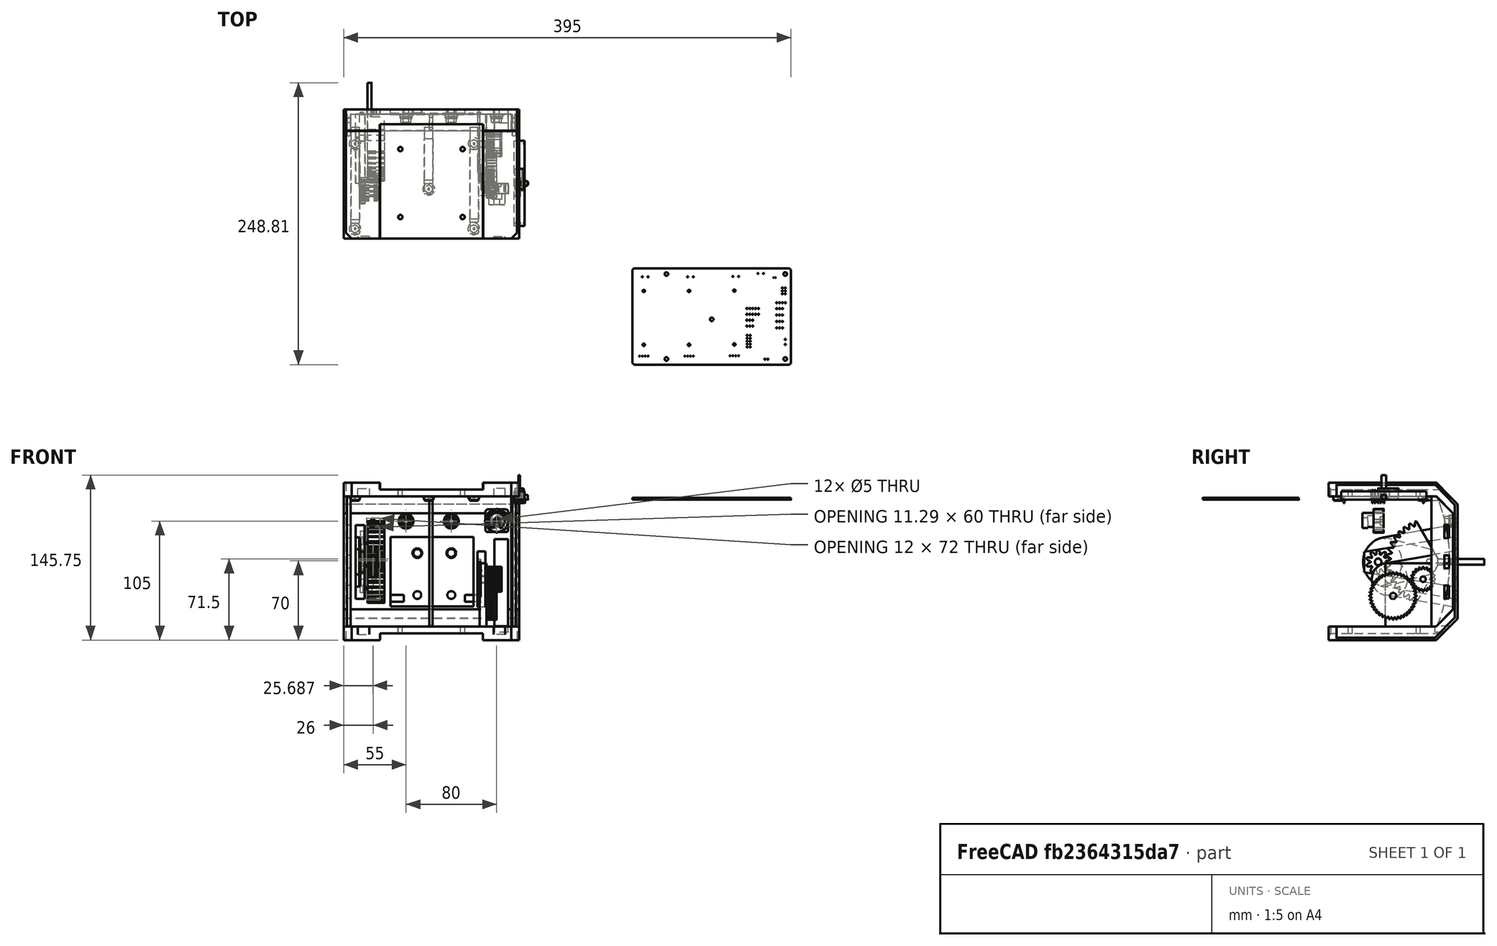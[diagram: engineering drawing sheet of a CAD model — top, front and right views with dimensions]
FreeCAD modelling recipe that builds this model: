
FCSTD DOCUMENT  (FreeCAD 0.19R24276 (Git))
Label: C152QuadrantCase
License: All rights reserved
LicenseURL: http://en.wikipedia.org/wiki/All_rights_reserved
objects: Sketcher::SketchObject×71, Part::Feature×60, App::Part×60, PartDesign::Pocket×42, PartDesign::Pad×29, PartDesign::Plane×15, PartDesign::Body×12, PartDesign::Fillet×10, PartDesign::Chamfer×8, Part::Part2DObjectPython×4, Mesh::Feature×3, PartDesign::ShapeBinder×2, PartDesign::LinearPattern×1, PartDesign::Line×1, PartDesign::PolarPattern×1
note: 345 computed .brp shape members not serialized (recipe doc carries the construction recipe); baked Part::Feature solids carry a one-line shape summary decoded from their .brp

FEATURE [Sketcher::SketchObject] Sketch
  FullyConstrained = false
  MapMode = 5
  Placement = pos=(0,0,0) rot=(0.57735,0.57735,0.57735;2.0944rad)
  Support = -> [YZ_Plane050]
  sketch-geometry (12):
    g0: LineSegment StartX=-48.736 StartY=3 StartZ=0 EndX=46.264 EndY=3 EndZ=0
    g1: LineSegment StartX=46.264 StartY=3 StartZ=0 EndX=61.264 EndY=-12 EndZ=0
    g2: LineSegment StartX=61.264 StartY=-12 StartZ=0 EndX=61.264 EndY=-97 EndZ=0
    g3: LineSegment StartX=61.264 StartY=-97 StartZ=0 EndX=46.264 EndY=-112 EndZ=0
    g4: LineSegment StartX=46.264 StartY=-112 StartZ=0 EndX=-48.736 EndY=-112 EndZ=0
    g5: LineSegment StartX=-48.736 StartY=3 StartZ=0 EndX=-48.736 EndY=15 EndZ=0
    g6: LineSegment StartX=-48.736 StartY=15 StartZ=0 EndX=46.264 EndY=15 EndZ=0
    g7: LineSegment StartX=46.264 StartY=15 StartZ=0 EndX=65.264 EndY=-4 EndZ=0
    g8: LineSegment StartX=65.264 StartY=-4 StartZ=0 EndX=65.264 EndY=-105 EndZ=0
    g9: LineSegment StartX=65.264 StartY=-105 StartZ=0 EndX=46.264 EndY=-124 EndZ=0
    g10: LineSegment StartX=46.264 StartY=-124 StartZ=0 EndX=-48.736 EndY=-124 EndZ=0
    g11: LineSegment StartX=-48.736 StartY=-124 StartZ=0 EndX=-48.736 EndY=-112 EndZ=0
  constraints (35):
    c: Horizontal(g0)
    c: Coincident(g1,g0)
    c: Coincident(g2,g1)
    c: Vertical(g2)
    c: Coincident(g3,g2)
    c: Coincident(g4,g3)
    c: Horizontal(g4)
    c: DistanceY(g2,g2) = 85
    c: DistanceY(g1,g0) = 15
    c: DistanceX(g0,g1) = 15
    c: DistanceY(g3,g2) = 15
    c: DistanceX(g3,g2) = 15
    c: DistanceX(g0,g0) = 95
    c: Equal(g0,g4)
    c: Coincident(g5,g0)
    c: Vertical(g5)
    c: Coincident(g6,g5)
    c: Horizontal(g6)
    c: Coincident(g7,g6)
    c: Coincident(g8,g7)
    c: Vertical(g8)
    c: Coincident(g9,g8)
    c: Coincident(g10,g9)
    c: Horizontal(g10)
    c: Coincident(g11,g4)
    c: Vertical(g11)
    c: Coincident(g11,g10)
    c: DistanceY(g11,g11) = 12
    c: Equal(g5,g11)
    c: Equal(g10,g4)
    c: Equal(g0,g6)
    c: DistanceX(g1,g7) = 4
    c: DistanceY(g-1,g0) = 3
    c: Parallel(g3,g9)
    c: Parallel(g1,g7)
FEATURE [PartDesign::Pad] Pad
  Direction = (1,1,1)
  Length = 155
  Length2 = 100
  Placement = pos=(0,0,0) rot=(0.57735,0.57735,0.57735;2.0944rad)
  Profile = -> Sketch
  Reversed = true
  Type = 0
FEATURE [Sketcher::SketchObject] Sketch001
  ExternalGeometry = -> [Pad]
  FullyConstrained = false
  MapMode = 5
  Placement = pos=(2.87e-14,65.264,-1.44e-14) rot=(0.57735,0.57735,0.57735;4.18879rad)
  Support = -> [Pad]
  sketch-geometry (39):
    g0: Circle CenterX=-19 CenterY=-20 CenterZ=0 NormalX=0 NormalY=0 NormalZ=1 AngleXU=0 Radius=2.5
    g1: LineSegment StartX=-9 StartY=-30 StartZ=0 EndX=-9 EndY=-10 EndZ=0
    g2: LineSegment StartX=-9 StartY=-10 StartZ=0 EndX=-29 EndY=-10 EndZ=0
    g3: LineSegment StartX=-29 StartY=-10 StartZ=0 EndX=-29 EndY=-30 EndZ=0
    g4: LineSegment StartX=-29 StartY=-30 StartZ=0 EndX=-9 EndY=-30 EndZ=0
    g5: Circle CenterX=-19 CenterY=-20 CenterZ=0 NormalX=0 NormalY=0 NormalZ=1 AngleXU=0 Radius=14.1421
    g6: Circle CenterX=-19 CenterY=-60 CenterZ=0 NormalX=0 NormalY=0 NormalZ=1 AngleXU=0 Radius=2.5
    g7: Circle CenterX=-19 CenterY=-100 CenterZ=0 NormalX=0 NormalY=0 NormalZ=1 AngleXU=0 Radius=2.5
    g8: LineSegment StartX=-117 StartY=-10 StartZ=0 EndX=-35.015 EndY=-10 EndZ=0
    g9: LineSegment StartX=-35.015 StartY=-10 StartZ=0 EndX=-35.015 EndY=-22 EndZ=0
    g10: LineSegment StartX=-35.015 StartY=-22 StartZ=0 EndX=-117 EndY=-22 EndZ=0
    g11: LineSegment StartX=-117 StartY=-22 StartZ=0 EndX=-117 EndY=-10 EndZ=0
    g12: Circle CenterX=-47.2303 CenterY=-60 CenterZ=0 NormalX=0 NormalY=0 NormalZ=1 AngleXU=0 Radius=4.25
    g13: Circle CenterX=-47.2303 CenterY=-90 CenterZ=0 NormalX=0 NormalY=0 NormalZ=1 AngleXU=0 Radius=4.25
    g14: LineSegment StartX=-16.5 StartY=-123 StartZ=0 EndX=-16.5 EndY=-135 EndZ=0
    g15: LineSegment StartX=-16.5 StartY=-135 StartZ=0 EndX=-88.5 EndY=-135 EndZ=0
    g16: LineSegment StartX=-88.5 StartY=-135 StartZ=0 EndX=-88.5 EndY=-129 EndZ=0
    g17: LineSegment StartX=-88.5 StartY=-129 StartZ=0 EndX=-70.5 EndY=-129 EndZ=0
    g18: LineSegment StartX=-70.5 StartY=-129 StartZ=0 EndX=-70.5 EndY=-126 EndZ=0
    g19: LineSegment StartX=-70.5 StartY=-126 StartZ=0 EndX=-52.5 EndY=-126 EndZ=0
    g20: LineSegment StartX=-52.5 StartY=-126 StartZ=0 EndX=-52.5 EndY=-123 EndZ=0
    g21: LineSegment StartX=-52.5 StartY=-123 StartZ=0 EndX=-34.5 EndY=-123 EndZ=0
    g22: LineSegment StartX=-34.5 StartY=-123 StartZ=0 EndX=-16.5 EndY=-123 EndZ=0
    g23: LineSegment StartX=-47.2303 StartY=-60 StartZ=0 EndX=-84.2303 EndY=-60 EndZ=0
    g24: LineSegment StartX=-84.2303 StartY=-60 StartZ=0 EndX=-84.2303 EndY=-90 EndZ=0
    g25: LineSegment StartX=-84.2303 StartY=-90 StartZ=0 EndX=-47.2303 EndY=-90 EndZ=0
    g26: LineSegment StartX=-47.2303 StartY=-90 StartZ=0 EndX=-47.2303 EndY=-60 EndZ=0
    g27: Circle CenterX=-84.2303 CenterY=-60 CenterZ=0 NormalX=0 NormalY=0 NormalZ=1 AngleXU=0 Radius=3.45
    g28: Circle CenterX=-84.2303 CenterY=-90 CenterZ=0 NormalX=0 NormalY=0 NormalZ=1 AngleXU=0 Radius=3.45
    g29: LineSegment StartX=-84.2303 StartY=-47.9735 StartZ=0 EndX=-90.2303 EndY=-47.9735 EndZ=0
    g30: LineSegment StartX=-90.2303 StartY=-47.9735 StartZ=0 EndX=-90.2303 EndY=-35.9735 EndZ=0
    g31: LineSegment StartX=-90.2303 StartY=-35.9735 StartZ=0 EndX=-84.2303 EndY=-35.9735 EndZ=0
    g32: LineSegment StartX=-84.2303 StartY=-35.9735 StartZ=0 EndX=-84.2303 EndY=-47.9735 EndZ=0
    g33: LineSegment StartX=-84.2303 StartY=-102.026 StartZ=0 EndX=-90.2303 EndY=-102.026 EndZ=0
    g34: LineSegment StartX=-90.2303 StartY=-102.026 StartZ=0 EndX=-90.2303 EndY=-114.026 EndZ=0
    g35: LineSegment StartX=-90.2303 StartY=-114.026 StartZ=0 EndX=-84.2303 EndY=-114.026 EndZ=0
    g36: LineSegment StartX=-84.2303 StartY=-114.026 StartZ=0 EndX=-84.2303 EndY=-102.026 EndZ=0
    g37: LineSegment StartX=-84.2303 StartY=-60 StartZ=0 EndX=-84.2303 EndY=-47.9735 EndZ=0
    g38: LineSegment StartX=-84.2303 StartY=-90 StartZ=0 EndX=-84.2303 EndY=-102.026 EndZ=0
  constraints (107):
    c: DistanceY(g0,g-4) = 20
    c: Coincident(g1,g2)
    c: Coincident(g2,g3)
    c: Coincident(g3,g4)
    c: Coincident(g4,g1)
    c: Equal(g1,g2)
    c: Equal(g1,g3)
    c: Equal(g1,g4)
    c: PointOnObject(g1,g5)
    c: PointOnObject(g2,g5)
    c: PointOnObject(g3,g5)
    c: PointOnObject(g4,g5)
    c: Coincident(g5,g0)
    c: Horizontal(g2)
    c: DistanceX(g0,g-4) = 15
    c: DistanceX(g4,g4) = 20
    c: Radius(g0) = 2.5
    c: Equal(g0,g6)
    c: Equal(g6,g7)
    c: DistanceX(g0,g6) = 0
    c: DistanceX(g6,g7) = 0
    c: DistanceY(g6,g0) = 40
    c: DistanceY(g7,g6) = 40
    c: Coincident(g8,g9)
    c: Coincident(g9,g10)
    c: Coincident(g10,g11)
    c: Coincident(g11,g8)
    c: Horizontal(g8)
    c: Horizontal(g10)
    c: Vertical(g9)
    c: Vertical(g11)
    c: DistanceX(g8,g-4) = 12
    c: DistanceY(g11,g11) = 12
    c: DistanceY(g8,g-4) = 10
    c: DistanceY(g12,g6) = 0
    c: DistanceX(g12,g13) = 0
    c: DistanceY(g13,g12) = 30
    c: Equal(g12,g13)
    c: Radius(g13) = 4.25
    c: Vertical(g14)
    c: Coincident(g15,g14)
    c: Horizontal(g15)
    c: Coincident(g16,g15)
    c: Vertical(g16)
    c: Coincident(g17,g16)
    c: Horizontal(g17)
    c: Vertical(g18)
    c: Coincident(g19,g18)
    c: Horizontal(g19)
    c: Coincident(g20,g19)
    c: Coincident(g21,g20)
    c: Horizontal(g21)
    c: Coincident(g22,g14)
    c: Horizontal(g22)
    c: Vertical(g20)
    c: Equal(g19,g21)
    c: Equal(g21,g22)
    c: Equal(g22,g17)
    c: Coincident(g17,g18)
    c: DistanceX(g15,g15) = 72
    c: DistanceY(g-3,g14) = 20
    c: DistanceX(g14,g-3) = 12.5
    c: Coincident(g21,g22)
    c: Equal(g18,g20)
    c: DistanceY(g18,g18) = 3
    c: DistanceY(g16,g16) = 6
    c: Coincident(g23,g24)
    c: Coincident(g24,g25)
    c: Coincident(g25,g26)
    c: Coincident(g26,g23)
    c: Horizontal(g23)
    c: Horizontal(g25)
    c: Vertical(g24)
    c: Coincident(g23,g12)
    c: Coincident(g25,g13)
    c: DistanceX(g23,g23) = 37
    c: Coincident(g27,g23)
    c: Coincident(g28,g24)
    c: Radius(g28) = 3.45
    c: Equal(g28,g27)
    c: Coincident(g29,g30)
    c: Coincident(g30,g31)
    c: Coincident(g31,g32)
    c: Coincident(g32,g29)
    c: Horizontal(g29)
    c: Horizontal(g31)
    c: Vertical(g30)
    c: Vertical(g32)
    c: Coincident(g33,g34)
    c: Coincident(g34,g35)
    c: Coincident(g35,g36)
    c: Coincident(g36,g33)
    c: Horizontal(g33)
    c: Horizontal(g35)
    c: Vertical(g34)
    c: Vertical(g36)
    c: Equal(g36,g32)
    c: Equal(g31,g33)
    c: Coincident(g37,g27)
    c: Coincident(g37,g29)
    c: Coincident(g38,g28)
    c: Coincident(g38,g33)
    c: Vertical(g38)
    c: Vertical(g37)
    c: Equal(g37,g38)
    c: DistanceY(g32,g32) = 12
    c: DistanceX(g31,g31) = 6
FEATURE [Mesh::Feature] Cessna_trim_wheel
  Placement = pos=(-19,36,-70) rot=(0,1,0;1.5708rad)
FEATURE [PartDesign::Pocket] Pocket
  BaseFeature = -> Pad
  Length = 20
  Length2 = 100
  Placement = pos=(0,0,0) rot=(0.57735,0.57735,0.57735;2.0944rad)
  Profile = -> Sketch001
  Type = 0
FEATURE [Sketcher::SketchObject] Sketch002
  AttachmentOffset = pos=(0,0,-120) rot=(0,0,1;0rad)
  ExternalGeometry = -> [Pocket]
  FullyConstrained = false
  MapMode = 5
  Placement = pos=(-35,7.5e-15,-7.5e-15) rot=(0.57735,0.57735,-0.57735;4.18879rad)
  Support = -> [Pocket]
  sketch-geometry (5):
    g0: LineSegment StartX=61.264 StartY=56.1492 StartZ=0 EndX=61.264 EndY=97 EndZ=0
    g1: LineSegment StartX=46.264 StartY=112 StartZ=0 EndX=1.26399 EndY=112 EndZ=0
    g2: LineSegment StartX=1.26399 StartY=112 StartZ=0 EndX=1.26399 EndY=56.1492 EndZ=0
    g3: LineSegment StartX=61.264 StartY=56.1492 StartZ=0 EndX=1.26399 EndY=56.1492 EndZ=0
    g4: LineSegment StartX=46.264 StartY=112 StartZ=0 EndX=61.264 EndY=97 EndZ=0
  constraints (12):
    c: PointOnObject(g0,g-3)
    c: Coincident(g0,g-4)
    c: Coincident(g1,g-5)
    c: Coincident(g2,g1)
    c: Vertical(g2)
    c: Coincident(g3,g0)
    c: Coincident(g3,g2)
    c: Horizontal(g3)
    c: DistanceX(g3,g3) = 60
    c: PointOnObject(g1,g-5)
    c: Coincident(g4,g1)
    c: Coincident(g4,g0)
FEATURE [PartDesign::Pad] Pad001
  BaseFeature = -> Pocket
  Direction = (1,1,1)
  Length = 6
  Length2 = 100
  Placement = pos=(0,0,0) rot=(0.57735,0.57735,0.57735;2.0944rad)
  Profile = -> Sketch002
  Reversed = true
  Type = 0
FEATURE [Part::Part2DObjectPython] InvoluteGear  label="TrimSmallGear"  # Draft 2D object (typed FeaturePython)
  ExternalGear = true
  HighPrecision = true
  Modules = 1
  NumberOfTeeth = 20
  Placement = pos=(-29,34.7,-70.25) rot=(0,1,0;1.5708rad)
  PressureAngle = 27
FEATURE [PartDesign::Pad] Pad002
  Direction = (1,1,1)
  Length = 13.5
  Length2 = 100
  Placement = pos=(-29,34.7,-70.25) rot=(0,1,0;1.5708rad)
  Profile = -> InvoluteGear
  Type = 0
FEATURE [Part::Part2DObjectPython] InvoluteGear001  # Draft 2D object (typed FeaturePython)
  ExternalGear = true
  HighPrecision = true
  Modules = 1
  NumberOfTeeth = 40
  Placement = pos=(-29,8.2,-85) rot=(0,1,0;1.5708rad)
  PressureAngle = 27
FEATURE [PartDesign::Pad] Pad003
  Direction = (1,1,1)
  Length = 9
  Length2 = 100
  Placement = pos=(-29,8.2,-85) rot=(0,1,0;1.5708rad)
  Profile = -> InvoluteGear001
  Type = 0
FEATURE [Sketcher::SketchObject] Sketch003
  FullyConstrained = true
  MapMode = 5
  Placement = pos=(-29,8.2,-85) rot=(0.707107,0,-0.707107;3.14159rad)
  Support = -> [Pad003]
  sketch-geometry (1):
    g0: Circle CenterX=0 CenterY=0 CenterZ=0 NormalX=0 NormalY=0 NormalZ=1 AngleXU=0 Radius=2.75
  constraints (2):
    c: Coincident(g0,g-1)
    c: Radius(g0) = 2.75
FEATURE [PartDesign::Pocket] Pocket001
  BaseFeature = -> Pad003
  Length = 10
  Length2 = 100
  Placement = pos=(-29,8.2,-85) rot=(0,1,0;1.5708rad)
  Profile = -> Sketch003
  Type = 0
FEATURE [PartDesign::Body] Body002  label="TrimLargeGearBody"
  Group = -> [InvoluteGear001,Pad003,Sketch003,Pocket001]
  Origin = -> Origin052
  Tip = -> Pocket001
FEATURE [Sketcher::SketchObject] Sketch004
  FullyConstrained = true
  MapMode = 5
  Placement = pos=(-15.5,34.7,-70.25) rot=(0,1,0;1.5708rad)
  Support = -> [Pad002]
  sketch-geometry (1):
    g0: Circle CenterX=0 CenterY=0 CenterZ=0 NormalX=0 NormalY=0 NormalZ=1 AngleXU=0 Radius=2.425
  constraints (2):
    c: Coincident(g0,g-1)
    c: Radius(g0) = 2.425
FEATURE [PartDesign::Pocket] Pocket002
  BaseFeature = -> Pad002
  Length = 15
  Length2 = 100
  Placement = pos=(-29,34.7,-70.25) rot=(0,1,0;1.5708rad)
  Profile = -> Sketch004
  Type = 0
FEATURE [PartDesign::Plane] DatumPlane
  AttachmentOffset = pos=(0,0,-13) rot=(0,0,1;0rad)
  Length = 88.036
  MapMode = 7
  Placement = pos=(-16,42.9375,-65.4383) rot=(0.57735,-0.57735,-0.57735;2.0944rad)
  ResizeMode = 0
  Support = -> [Pocket002]
  Width = 123.586
FEATURE [PartDesign::Body] Body  label="TrimSmallGearBody"
  Group = -> [InvoluteGear,Pad002,Sketch004,Pocket002,DatumPlane]
  Origin = -> Origin051
  Tip = -> Pocket002
FEATURE [Mesh::Feature] Mesh  label="TrimSmallGearBody (Meshed)"
FEATURE [Mesh::Feature] Union
FEATURE [Part::Part2DObjectPython] InvoluteGear002  # Draft 2D object (typed FeaturePython)
  ExternalGear = true
  HighPrecision = true
  Modules = 1.8
  NumberOfTeeth = 40
  Placement = pos=(-134,40,-55) rot=(0,1,0;1.5708rad)
  PressureAngle = 27
FEATURE [PartDesign::Pad] Pad004
  Direction = (1,1,1)
  Length = 15
  Length2 = 100
  Placement = pos=(-134,40,-55) rot=(0,1,0;1.5708rad)
  Profile = -> InvoluteGear002
  Type = 0
FEATURE [Sketcher::SketchObject] Sketch005
  ExternalGeometry = -> [Pad004]
  FullyConstrained = false
  MapMode = 5
  Placement = pos=(-134,40,-55) rot=(0.707107,0,-0.707107;3.14159rad)
  Support = -> [Pad004]
  sketch-geometry (9):
    g0: Circle CenterX=0 CenterY=0 CenterZ=0 NormalX=0 NormalY=0 NormalZ=1 AngleXU=0 Radius=2.5
    g1: LineSegment StartX=-36.0831 StartY=11.2641 StartZ=0 EndX=-2.5 EndY=-7.97211 EndZ=0
    g2: LineSegment StartX=36.0831 StartY=11.2641 StartZ=0 EndX=2.5 EndY=-7.97211 EndZ=0
    g3: LineSegment StartX=-36.0831 StartY=11.2641 StartZ=0 EndX=-54.9276 EndY=-6.77916 EndZ=0
    g4: LineSegment StartX=-54.9276 StartY=-6.77916 StartZ=0 EndX=-2.5 EndY=-49.2175 EndZ=0
    g5: LineSegment StartX=-2.5 StartY=-49.2175 StartZ=0 EndX=-2.5 EndY=-7.97211 EndZ=0
    g6: LineSegment StartX=2.5 StartY=-7.97211 StartZ=0 EndX=2.5 EndY=-49.2175 EndZ=0
    g7: LineSegment StartX=2.5 StartY=-49.2175 StartZ=0 EndX=46.3022 EndY=-15.9819 EndZ=0
    g8: LineSegment StartX=46.3022 StartY=-15.9819 StartZ=0 EndX=36.0831 EndY=11.2641 EndZ=0
  constraints (16):
    c: Coincident(g0,g-1)
    c: Radius(g0) = 2.5
    c: Coincident(g1,g-3)
    c: Coincident(g2,g-4)
    c: Symmetric(g1,g2,g-2)
    c: Coincident(g3,g1)
    c: Coincident(g4,g3)
    c: Coincident(g5,g4)
    c: Coincident(g5,g1)
    c: Vertical(g5)
    c: Coincident(g6,g2)
    c: Coincident(g7,g6)
    c: Coincident(g8,g7)
    c: Coincident(g8,g2)
    c: Symmetric(g4,g6,g-2)
    c: DistanceX(g1,g2) = 5
FEATURE [PartDesign::Pocket] Pocket003
  BaseFeature = -> Pad004
  Length = 20
  Length2 = 100
  Placement = pos=(-134,40,-55) rot=(0,1,0;1.5708rad)
  Profile = -> Sketch005
  Type = 0
FEATURE [Sketcher::SketchObject] Sketch006
  ExternalGeometry = -> [Pocket003]
  FullyConstrained = true
  MapMode = 5
  Placement = pos=(-134,40,-55) rot=(0.707107,0,-0.707107;3.14159rad)
  Support = -> [Pocket003]
  sketch-geometry (4):
    g0: LineSegment StartX=-2.5 StartY=-33.8136 StartZ=0 EndX=2.5 EndY=-33.8136 EndZ=0
    g1: LineSegment StartX=2.5 StartY=-33.8136 StartZ=0 EndX=2.5 EndY=-48.8136 EndZ=0
    g2: LineSegment StartX=2.5 StartY=-48.8136 StartZ=0 EndX=-2.5 EndY=-48.8136 EndZ=0
    g3: LineSegment StartX=-2.5 StartY=-48.8136 StartZ=0 EndX=-2.5 EndY=-33.8136 EndZ=0
  constraints (10):
    c: Coincident(g0,g1)
    c: Coincident(g1,g2)
    c: Coincident(g2,g3)
    c: Coincident(g3,g0)
    c: Horizontal(g2)
    c: Vertical(g1)
    c: Vertical(g3)
    c: Coincident(g0,g-3)
    c: Coincident(g0,g-4)
    c: DistanceY(g1,g1) = 15
FEATURE [PartDesign::Pad] Pad005
  BaseFeature = -> Pocket003
  Direction = (1,1,1)
  Length = 15
  Length2 = 100
  Placement = pos=(-134,40,-55) rot=(0,1,0;1.5708rad)
  Profile = -> Sketch006
  Reversed = true
  Type = 0
FEATURE [Part::Part2DObjectPython] InvoluteGear003  # Draft 2D object (typed FeaturePython)
  ExternalGear = true
  HighPrecision = true
  Modules = 1.8
  NumberOfTeeth = 10
  Placement = pos=(-140,-5,-55) rot=(0,1,0;1.5708rad)
  PressureAngle = 27
FEATURE [PartDesign::Pad] Pad006
  Direction = (1,1,1)
  Length = 15
  Length2 = 100
  Placement = pos=(-140,-5,-55) rot=(0,1,0;1.5708rad)
  Profile = -> InvoluteGear003
  Type = 0
FEATURE [Sketcher::SketchObject] Sketch008
  ExternalGeometry = -> [Pad005]
  FullyConstrained = false
  MapMode = 5
  Placement = pos=(-134,88.8136,-55) rot=(0.57735,0.57735,0.57735;4.18879rad)
  Support = -> [Pad005]
  sketch-geometry (4):
    g0: LineSegment StartX=2.5 StartY=15 StartZ=0 EndX=-2.5 EndY=15 EndZ=0
    g1: LineSegment StartX=-2.5 StartY=15 StartZ=0 EndX=-2.5 EndY=3.5 EndZ=0
    g2: LineSegment StartX=-2.5 StartY=3.5 StartZ=0 EndX=2.5 EndY=3.5 EndZ=0
    g3: LineSegment StartX=2.5 StartY=3.5 StartZ=0 EndX=2.5 EndY=15 EndZ=0
  constraints (10):
    c: Coincident(g0,g1)
    c: Coincident(g1,g2)
    c: Coincident(g2,g3)
    c: Coincident(g3,g0)
    c: Horizontal(g2)
    c: Vertical(g1)
    c: Vertical(g3)
    c: Coincident(g0,g-4)
    c: Coincident(g0,g-3)
    c: DistanceY(g-5,g1) = 3.5
FEATURE [PartDesign::Pocket] Pocket005
  BaseFeature = -> Pad005
  Length = 30
  Length2 = 100
  Placement = pos=(-134,40,-55) rot=(0,1,0;1.5708rad)
  Profile = -> Sketch008
  Type = 0
FEATURE [PartDesign::Fillet] Fillet
  Base = -> Pocket005 [Edge322,Edge311,Edge323,Edge301]
  BaseFeature = -> Pocket005
  Placement = pos=(-134,40,-55) rot=(0,1,0;1.5708rad)
  Radius = 1.5
  SupportTransform = false
FEATURE [PartDesign::Body] Body003  label="FlapsLeverWheel"
  Group = -> [InvoluteGear002,Pad004,Sketch005,Pocket003,Sketch006,Pad005,Sketch008,Pocket005,Fillet]
  Origin = -> Origin053
  Tip = -> Fillet
FEATURE [Sketcher::SketchObject] Sketch009
  FullyConstrained = true
  MapMode = 5
  Placement = pos=(-140,-5,-55) rot=(0.707107,0,-0.707107;3.14159rad)
  Support = -> [Pad006]
  sketch-geometry (1):
    g0: Circle CenterX=0 CenterY=0 CenterZ=0 NormalX=0 NormalY=0 NormalZ=1 AngleXU=0 Radius=2.875
  constraints (2):
    c: Coincident(g0,g-1)
    c: Radius(g0) = 2.875
FEATURE [PartDesign::Pocket] Pocket006
  BaseFeature = -> Pad006
  Length = 20
  Length2 = 100
  Placement = pos=(-140,-5,-55) rot=(0,1,0;1.5708rad)
  Profile = -> Sketch009
  Type = 0
FEATURE [PartDesign::Body] Body004  label="FlapsPotWheel"
  Group = -> [InvoluteGear003,Pad006,Sketch009,Pocket006]
  Origin = -> Origin054
  Tip = -> Pocket006
FEATURE [Sketcher::SketchObject] Sketch010
  AttachmentOffset = pos=(0,0,-19) rot=(0,0,1;0rad)
  ExternalGeometry = -> [Pad001]
  FullyConstrained = false
  MapMode = 5
  Placement = pos=(-136,2.99e-14,-2.99e-14) rot=(0.57735,0.57735,-0.57735;4.18879rad)
  Support = -> [Pad001]
  sketch-geometry (7):
    g0: LineSegment StartX=-17.4237 StartY=64.0314 StartZ=0 EndX=61.264 EndY=76.6336 EndZ=0
    g1: LineSegment StartX=61.264 StartY=33.3706 StartZ=0 EndX=61.264 EndY=76.6336 EndZ=0
    g2: LineSegment StartX=61.264 StartY=33.3706 StartZ=0 EndX=-17.4237 EndY=45.9729 EndZ=0
    g3: LineSegment StartX=-17.4237 StartY=45.9729 StartZ=0 EndX=-17.4237 EndY=64.0314 EndZ=0
    g4: LineSegment StartX=94.0604 StartY=55.0021 StartZ=0 EndX=-36.649 EndY=55.0021 EndZ=0
    g5: Circle CenterX=-5.01144 CenterY=55.0021 CenterZ=0 NormalX=0 NormalY=0 NormalZ=1 AngleXU=0 Radius=3.00681
    g6: Circle CenterX=39.9756 CenterY=55.0021 CenterZ=0 NormalX=0 NormalY=0 NormalZ=1 AngleXU=0 Radius=2.57688
  constraints (17):
    c: PointOnObject(g0,g-3)
    c: PointOnObject(g1,g-3)
    c: Coincident(g1,g0)
    c: Vertical(g1)
    c: Coincident(g2,g1)
    c: Coincident(g3,g2)
    c: Coincident(g3,g0)
    c: Vertical(g3)
    c: Horizontal(g4)
    c: Symmetric(g2,g0,g4)
    c: Symmetric(g1,g0,g4)
    c: PointOnObject(g5,g4)
    c: PointOnObject(g6,g4)
    c: Symmetric(g0,g2,g4)
    c: PointOnObject(g0,g-4)
    c: PointOnObject(g1,g-4)
    c: Symmetric(g0,g1,g4)
FEATURE [PartDesign::Pad] Pad007
  BaseFeature = -> Pad001
  Direction = (1,1,1)
  Length = 5.5
  Length2 = 100
  Placement = pos=(0,0,0) rot=(0.57735,0.57735,0.57735;2.0944rad)
  Profile = -> Sketch010
  Type = 0
FEATURE [Part::Feature] Part__Feature  label="SOLID"
  shape: bbox 9.2 x 75 x 24.75 mm, 23 faces (baked)
FEATURE [App::Part] ALPS_RS6011SY_Body  label="ALPS-RS6011SY-Body"
  Group = -> [Part__Feature]
  Origin = -> Origin055
  Placement = pos=(190,-117.2,1.65) rot=(0,0,1;0rad)
FEATURE [Part::Feature] Part__Feature001  label="SOLID001"
  shape: bbox 9.2 x 75 x 24.75 mm, 23 faces (baked)
FEATURE [App::Part] ALPS_RS6011SY_Body001  label="ALPS-RS6011SY-Body001"
  Group = -> [Part__Feature001]
  Origin = -> Origin056
  Placement = pos=(110,-117.5,1.65) rot=(0,0,1;0rad)
FEATURE [Part::Feature] Part__Feature002  label="SOLID002"
  shape: bbox 9.2 x 75 x 24.75 mm, 23 faces (baked)
FEATURE [App::Part] ALPS_RS6011SY_Body002  label="ALPS-RS6011SY-Body002"
  Group = -> [Part__Feature002]
  Origin = -> Origin057
  Placement = pos=(150,-117.5,1.65) rot=(0,0,1;0rad)
FEATURE [Part::Feature] Part__Feature003  label="SOLID003"
  shape: bbox 1.6 x 0.8 x 0.8 mm, 28 faces (baked)
FEATURE [App::Part] C_0603_1608Metric
  Group = -> [Part__Feature003]
  Origin = -> Origin058
  Placement = pos=(119.5,-86,1.65) rot=(0,0,1;0rad)
FEATURE [Part::Feature] Part__Feature004  label="SOLID004"
  shape: bbox 1.6 x 0.8 x 0.8 mm, 28 faces (baked)
FEATURE [App::Part] C_0603_1608Metric001
  Group = -> [Part__Feature004]
  Origin = -> Origin059
  Placement = pos=(213,-120.6,1.65) rot=(0,0,-1;1.5708rad)
FEATURE [Part::Feature] Part__Feature005  label="SOLID005"
  shape: bbox 1.6 x 0.8 x 0.8 mm, 28 faces (baked)
FEATURE [App::Part] C_0603_1608Metric002
  Group = -> [Part__Feature005]
  Origin = -> Origin060
  Placement = pos=(119.5,-90.75,1.65) rot=(0,0,1;0rad)
FEATURE [Part::Feature] Part__Feature006  label="SOLID006"
  shape: bbox 1.6 x 0.8 x 0.8 mm, 28 faces (baked)
FEATURE [App::Part] C_0603_1608Metric003
  Group = -> [Part__Feature006]
  Origin = -> Origin061
  Placement = pos=(210.4,-120.6,1.65) rot=(0,0,-1;1.5708rad)
FEATURE [Part::Feature] Part__Feature007  label="SOLID007"
  shape: bbox 1.6 x 0.8 x 0.8 mm, 28 faces (baked)
FEATURE [App::Part] C_0603_1608Metric004
  Group = -> [Part__Feature007]
  Origin = -> Origin062
  Placement = pos=(161.2,-83.2,1.65) rot=(0,0,1;0rad)
FEATURE [Part::Feature] Part__Feature008  label="SOLID008"
  shape: bbox 1.6 x 0.8 x 0.8 mm, 28 faces (baked)
FEATURE [App::Part] C_0603_1608Metric005
  Group = -> [Part__Feature008]
  Origin = -> Origin063
  Placement = pos=(161.2,-87.4,1.65) rot=(0,0,1;0rad)
FEATURE [Part::Feature] Part__Feature009  label="SOLID009"
  shape: bbox 1.6 x 0.8 x 0.8 mm, 28 faces (baked)
FEATURE [App::Part] C_0603_1608Metric006
  Group = -> [Part__Feature009]
  Origin = -> Origin064
  Placement = pos=(210.4,-125.6,1.65) rot=(0,0,-1;1.5708rad)
FEATURE [Part::Feature] Part__Feature010  label="SOLID010"
  shape: bbox 1.6 x 0.8 x 0.8 mm, 28 faces (baked)
FEATURE [App::Part] C_0603_1608Metric007
  Group = -> [Part__Feature010]
  Origin = -> Origin065
  Placement = pos=(213.2,-125.6,1.65) rot=(0,0,-1;1.5708rad)
FEATURE [Part::Feature] Part__Feature011  label="SOLID011"
  shape: bbox 1.6 x 0.8 x 0.8 mm, 28 faces (baked)
FEATURE [App::Part] C_0603_1608Metric008
  Group = -> [Part__Feature011]
  Origin = -> Origin066
  Placement = pos=(182,-143,1.65) rot=(0,0,1;3.14159rad)
FEATURE [Part::Feature] Part__Feature012  label="SOLID012"
  shape: bbox 1.6 x 0.8 x 0.8 mm, 28 faces (baked)
FEATURE [App::Part] C_0603_1608Metric009
  Group = -> [Part__Feature012]
  Origin = -> Origin067
  Placement = pos=(182,-146.6,1.65) rot=(0,0,1;3.14159rad)
FEATURE [Part::Feature] Part__Feature013  label="SOLID013"
  shape: bbox 1.6 x 0.8 x 0.8 mm, 28 faces (baked)
FEATURE [App::Part] C_0603_1608Metric010
  Group = -> [Part__Feature013]
  Origin = -> Origin068
  Placement = pos=(218.4,-84.4,1.65) rot=(0,0,1;0rad)
FEATURE [Part::Feature] Part__Feature014  label="SOLID014"
  shape: bbox 1.6 x 0.8 x 0.8 mm, 28 faces (baked)
FEATURE [App::Part] C_0603_1608Metric011
  Group = -> [Part__Feature014]
  Origin = -> Origin069
  Placement = pos=(208.6,-84.4,1.65) rot=(0,0,1;0rad)
FEATURE [Part::Feature] Part__Feature015  label="SOLID015"
  shape: bbox 1.6 x 0.8 x 0.8 mm, 28 faces (baked)
FEATURE [App::Part] C_0603_1608Metric012
  Group = -> [Part__Feature015]
  Origin = -> Origin070
  Placement = pos=(227.35,-85.9,1.65) rot=(0,0,1;0rad)
FEATURE [Part::Feature] Part__Feature016  label="SOLID016"
  shape: bbox 1.6 x 0.8 x 0.8 mm, 28 faces (baked)
FEATURE [App::Part] C_0603_1608Metric013
  Group = -> [Part__Feature016]
  Origin = -> Origin071
  Placement = pos=(223.85,-85.9,1.65) rot=(0,0,1;3.14159rad)
FEATURE [Part::Feature] Part__Feature017  label="SOLID017"
  shape: bbox 1.6 x 0.8 x 0.8 mm, 28 faces (baked)
FEATURE [App::Part] C_0603_1608Metric014
  Group = -> [Part__Feature017]
  Origin = -> Origin072
  Placement = pos=(177.5,-83.25,1.65) rot=(0,0,1;0rad)
FEATURE [Part::Feature] Part__Feature018  label="SOLID018"
  shape: bbox 1.6 x 0.8 x 0.8 mm, 28 faces (baked)
FEATURE [App::Part] C_0603_1608Metric015
  Group = -> [Part__Feature018]
  Origin = -> Origin073
  Placement = pos=(220.938,-105,1.65) rot=(0,0,1;0rad)
FEATURE [Part::Feature] Part__Feature019  label="SOLID019"
  shape: bbox 1.6 x 0.8 x 0.8 mm, 28 faces (baked)
FEATURE [App::Part] C_0603_1608Metric016
  Group = -> [Part__Feature019]
  Origin = -> Origin074
  Placement = pos=(211.2,-98.2,1.65) rot=(0,0,-1;1.5708rad)
FEATURE [Part::Feature] Part__Feature020  label="SOLID020"
  shape: bbox 1.6 x 0.8 x 0.8 mm, 28 faces (baked)
FEATURE [App::Part] C_0603_1608Metric017
  Group = -> [Part__Feature020]
  Origin = -> Origin075
  Placement = pos=(212.2,-88.6,1.65) rot=(0,0,1;3.14159rad)
FEATURE [Part::Feature] Part__Feature021  label="SOLID021"
  shape: bbox 1.6 x 0.8 x 0.8 mm, 28 faces (baked)
FEATURE [App::Part] C_0603_1608Metric018
  Group = -> [Part__Feature021]
  Origin = -> Origin076
  Placement = pos=(228.6,-93.8,1.65) rot=(0,0,1;1.5708rad)
FEATURE [Part::Feature] Part__Feature022  label="SOLID022"
  shape: bbox 2.54 x 7.62 x 11.54 mm, 76 faces (baked)
FEATURE [App::Part] PinHeader_1x03_P2_54mm_Vertical  label="PinHeader_1x03_P2.54mm_Vertical"
  Group = -> [Part__Feature022]
  Origin = -> Origin077
  Placement = pos=(232.5,-110.6,1.65) rot=(0,0,-1;1.5708rad)
FEATURE [Part::Feature] Part__Feature023  label="SOLID023"
  shape: bbox 2.54 x 7.62 x 11.54 mm, 76 faces (baked)
FEATURE [App::Part] PinHeader_1x03_P2_54mm_Vertical001  label="PinHeader_1x03_P2.54mm_Vertical001"
  Group = -> [Part__Feature023]
  Origin = -> Origin078
  Placement = pos=(232.5,-116.267,1.65) rot=(0,0,-1;1.5708rad)
FEATURE [Part::Feature] Part__Feature024  label="SOLID024"
  shape: bbox 2.54 x 7.62 x 11.54 mm, 76 faces (baked)
FEATURE [App::Part] PinHeader_1x03_P2_54mm_Vertical002  label="PinHeader_1x03_P2.54mm_Vertical002"
  Group = -> [Part__Feature024]
  Origin = -> Origin079
  Placement = pos=(232.5,-121.933,1.65) rot=(0,0,-1;1.5708rad)
FEATURE [Part::Feature] Part__Feature025  label="SOLID025"
  shape: bbox 2.54 x 7.62 x 11.54 mm, 76 faces (baked)
FEATURE [App::Part] PinHeader_1x03_P2_54mm_Vertical003  label="PinHeader_1x03_P2.54mm_Vertical003"
  Group = -> [Part__Feature025]
  Origin = -> Origin080
  Placement = pos=(232.5,-127.6,1.65) rot=(0,0,-1;1.5708rad)
FEATURE [Part::Feature] Part__Feature026  label="SOLID026"
  shape: bbox 5.08 x 7.62 x 11.54 mm, 130 faces (baked)
FEATURE [App::Part] PinHeader_2x03_P2_54mm_Vertical  label="PinHeader_2x03_P2.54mm_Vertical"
  Group = -> [Part__Feature026]
  Origin = -> Origin081
  Placement = pos=(232.4,-92.4,1.65) rot=(0,0,1;0rad)
FEATURE [Part::Feature] Part__Feature027  label="SOLID027"
  shape: bbox 2.54 x 5.08 x 11.54 mm, 52 faces (baked)
FEATURE [App::Part] PinHeader_1x02_P2_54mm_Vertical  label="PinHeader_1x02_P2.54mm_Vertical"
  Group = -> [Part__Feature027]
  Origin = -> Origin082
  Placement = pos=(219.6,-155.2,1.65) rot=(0,0,-1;1.5708rad)
FEATURE [Part::Feature] Part__Feature028  label="SOLID028"
  shape: bbox 1.6 x 0.8 x 0.45 mm, 26 faces (baked)
FEATURE [App::Part] R_0603_1608Metric
  Group = -> [Part__Feature028]
  Origin = -> Origin083
  Placement = pos=(216,-150.6,1.65) rot=(0,0,1;1.5708rad)
FEATURE [Part::Feature] Part__Feature029  label="SOLID029"
  shape: bbox 1.6 x 0.8 x 0.45 mm, 26 faces (baked)
FEATURE [App::Part] R_0603_1608Metric001
  Group = -> [Part__Feature029]
  Origin = -> Origin084
  Placement = pos=(177.6,-87.2,1.65) rot=(0,0,1;3.14159rad)
FEATURE [Part::Feature] Part__Feature030  label="SOLID030"
  shape: bbox 1.6 x 0.8 x 0.45 mm, 26 faces (baked)
FEATURE [App::Part] R_0603_1608Metric002
  Group = -> [Part__Feature030]
  Origin = -> Origin085
  Placement = pos=(213.6,-84.4,1.65) rot=(0,0,1;3.14159rad)
FEATURE [Part::Feature] Part__Feature031  label="SOLID031"
  shape: bbox 1.6 x 0.8 x 0.45 mm, 26 faces (baked)
FEATURE [App::Part] R_0603_1608Metric003
  Group = -> [Part__Feature031]
  Origin = -> Origin086
  Placement = pos=(231.4,-88.2,1.65) rot=(0,0,1;1.5708rad)
FEATURE [Part::Feature] Part__Feature032  label="SOLID032"
  shape: bbox 1.6 x 0.8 x 0.45 mm, 26 faces (baked)
FEATURE [App::Part] R_0603_1608Metric004
  Group = -> [Part__Feature032]
  Origin = -> Origin087
  Placement = pos=(236,-88,1.65) rot=(0,0,-1;1.5708rad)
FEATURE [Part::Feature] Part__Feature033  label="SOLID033"
  shape: bbox 1.6 x 0.8 x 0.45 mm, 26 faces (baked)
FEATURE [App::Part] R_0603_1608Metric005
  Group = -> [Part__Feature033]
  Origin = -> Origin088
  Placement = pos=(225.5,-138.5,1.65) rot=(0,0,-1;1.5708rad)
FEATURE [Part::Feature] Part__Feature034  label="SOLID034"
  shape: bbox 1.6 x 0.8 x 0.45 mm, 26 faces (baked)
FEATURE [App::Part] R_0603_1608Metric006
  Group = -> [Part__Feature034]
  Origin = -> Origin089
  Placement = pos=(222.25,-138.5,1.65) rot=(0,0,-1;1.5708rad)
FEATURE [Part::Feature] Part__Feature035  label="SOLID035"
  shape: bbox 1.6 x 0.8 x 0.45 mm, 26 faces (baked)
FEATURE [App::Part] R_0603_1608Metric007
  Group = -> [Part__Feature035]
  Origin = -> Origin090
  Placement = pos=(225.5,-134.8,1.65) rot=(0,0,1;1.5708rad)
FEATURE [Part::Feature] Part__Feature036  label="SOLID036"
  shape: bbox 2.54 x 7.62 x 11.54 mm, 76 faces (baked)
FEATURE [App::Part] PinHeader_1x03_P2_54mm_Vertical004  label="PinHeader_1x03_P2.54mm_Vertical004"
  Group = -> [Part__Feature036]
  Origin = -> Origin091
  Placement = pos=(206.25,-125.95,1.65) rot=(0,0,-1;1.5708rad)
FEATURE [Part::Feature] Part__Feature037  label="SOLID037"
  shape: bbox 2.54 x 7.62 x 11.54 mm, 76 faces (baked)
FEATURE [App::Part] PinHeader_1x03_P2_54mm_Vertical005  label="PinHeader_1x03_P2.54mm_Vertical005"
  Group = -> [Part__Feature037]
  Origin = -> Origin092
  Placement = pos=(206.25,-120.783,1.65) rot=(0,0,-1;1.5708rad)
FEATURE [Part::Feature] Part__Feature038  label="SOLID038"
  shape: bbox 2.54 x 10.16 x 11.54 mm, 100 faces (baked)
FEATURE [App::Part] PinHeader_1x04_P2_54mm_Vertical  label="PinHeader_1x04_P2.54mm_Vertical"
  Group = -> [Part__Feature038]
  Origin = -> Origin093
  Placement = pos=(227.4,-105.4,1.65) rot=(0,0,1;1.5708rad)
FEATURE [Part::Feature] Part__Feature039  label="SOLID039"
  shape: bbox 9 x 9 x 1.5 mm, 764 faces (baked)
FEATURE [App::Part] LQFP_48_7x7mm_P0_5mm  label="LQFP-48_7x7mm_P0.5mm"
  Group = -> [Part__Feature039]
  Origin = -> Origin094
  Placement = pos=(217.4,-96,1.65) rot=(0,0,-1;1.5708rad)
FEATURE [Part::Feature] Part__Feature040  label="SOLID040"
  shape: bbox 2.8 x 2.9 x 1.55 mm, 109 faces (baked)
FEATURE [App::Part] SOT_23_5  label="SOT-23-5"
  Group = -> [Part__Feature040]
  Origin = -> Origin095
  Placement = pos=(223,-145,1.65) rot=(0,0,1;3.14159rad)
FEATURE [Part::Feature] Part__Feature041  label="SOLID041"
  shape: bbox 11.05 x 4.65 x 7 mm, 26 faces (baked)
FEATURE [App::Part] Crystal_HC49_4H_Vertical  label="Crystal_HC49-4H_Vertical"
  Group = -> [Part__Feature041]
  Origin = -> Origin096
  Placement = pos=(215.75,-79.55,1.65) rot=(0,0,1;3.14159rad)
FEATURE [Part::Feature] Part__Feature042  label="SOLID042"
  shape: bbox 1.6 x 0.8 x 0.8 mm, 28 faces (baked)
FEATURE [App::Part] C_0603_1608Metric019
  Group = -> [Part__Feature042]
  Origin = -> Origin097
  Placement = pos=(162.2,-103.2,1.65) rot=(0,0,1;1.5708rad)
FEATURE [Part::Feature] Part__Feature043  label="SOLID043"
  shape: bbox 1.6 x 0.8 x 0.8 mm, 28 faces (baked)
FEATURE [App::Part] C_0603_1608Metric020
  Group = -> [Part__Feature043]
  Origin = -> Origin098
  Placement = pos=(162.4,-134.8,1.65) rot=(0,0,1;1.5708rad)
FEATURE [Part::Feature] Part__Feature044  label="SOLID044"
  shape: bbox 2.54 x 12.7 x 11.54 mm, 124 faces (baked)
FEATURE [App::Part] PinHeader_1x05_P2_54mm_Vertical  label="PinHeader_1x05_P2.54mm_Vertical"
  Group = -> [Part__Feature044]
  Origin = -> Origin099
  Placement = pos=(211.35,-110.45,1.65) rot=(0,0,-1;1.5708rad)
FEATURE [Part::Feature] Part__Feature045  label="SOLID045"
  shape: bbox 2.54 x 12.7 x 11.54 mm, 124 faces (baked)
FEATURE [App::Part] PinHeader_1x05_P2_54mm_Vertical001  label="PinHeader_1x05_P2.54mm_Vertical001"
  Group = -> [Part__Feature045]
  Origin = -> Origin100
  Placement = pos=(211.35,-115.617,1.65) rot=(0,0,-1;1.5708rad)
FEATURE [Part::Feature] Part__Feature046  label="SOLID046"
  shape: bbox 2.5 x 3 x 1.2 mm, 76 faces (baked)
FEATURE [App::Part] SOT_23  label="SOT-23"
  Group = -> [Part__Feature046]
  Origin = -> Origin101
  Placement = pos=(157.6,-107.4,1.65) rot=(0,0,1;3.14159rad)
FEATURE [Part::Feature] Part__Feature047  label="SOLID047"
  shape: bbox 2.5 x 3 x 1.2 mm, 76 faces (baked)
FEATURE [App::Part] SOT_23001  label="SOT-024"
  Group = -> [Part__Feature047]
  Origin = -> Origin102
  Placement = pos=(158.4,-137.8,1.65) rot=(0,0,1;3.14159rad)
FEATURE [Part::Feature] Part__Feature048  label="SOLID048"
  shape: bbox 1.6 x 0.8 x 0.45 mm, 26 faces (baked)
FEATURE [App::Part] R_0603_1608Metric008
  Group = -> [Part__Feature048]
  Origin = -> Origin103
  Placement = pos=(162.4,-112.8,1.65) rot=(0,0,-1;1.5708rad)
FEATURE [Part::Feature] Part__Feature049  label="SOLID049"
  shape: bbox 1.6 x 0.8 x 0.45 mm, 26 faces (baked)
FEATURE [App::Part] R_0603_1608Metric009
  Group = -> [Part__Feature049]
  Origin = -> Origin104
  Placement = pos=(162.25,-108,1.65) rot=(0,0,-1;1.5708rad)
FEATURE [Part::Feature] Part__Feature050  label="SOLID050"
  shape: bbox 1.6 x 0.8 x 0.45 mm, 26 faces (baked)
FEATURE [App::Part] R_0603_1608Metric010
  Group = -> [Part__Feature050]
  Origin = -> Origin105
  Placement = pos=(162.6,-143.6,1.65) rot=(0,0,-1;1.5708rad)
FEATURE [Part::Feature] Part__Feature051  label="SOLID051"
  shape: bbox 1.6 x 0.8 x 0.45 mm, 26 faces (baked)
FEATURE [App::Part] R_0603_1608Metric011
  Group = -> [Part__Feature051]
  Origin = -> Origin106
  Placement = pos=(162.45,-139.2,1.65) rot=(0,0,-1;1.5708rad)
FEATURE [Part::Feature] Part__Feature052  label="SOLID052"
  shape: bbox 3.2 x 1.6 x 1.6 mm, 28 faces (baked)
FEATURE [App::Part] C_1206_3216Metric
  Group = -> [Part__Feature052]
  Origin = -> Origin107
  Placement = pos=(227.4,-147.2,1.65) rot=(0,0,1;1.5708rad)
FEATURE [Part::Feature] Part__Feature053  label="SOLID053"
  shape: bbox 3.2 x 1.6 x 1.6 mm, 28 faces (baked)
FEATURE [App::Part] C_1206_3216Metric001
  Group = -> [Part__Feature053]
  Origin = -> Origin108
  Placement = pos=(223.2,-150,1.65) rot=(0,0,1;3.14159rad)
FEATURE [Part::Feature] Part__Feature054  label="SOLID054"
  shape: bbox 5.08 x 12.7 x 10.1 mm, 320 faces (baked)
FEATURE [App::Part] PinSocket_2x05_P2_54mm_Vertical  label="PinSocket_2x05_P2.54mm_Vertical"
  Group = -> [Part__Feature054]
  Origin = -> Origin109
  Placement = pos=(204,-134.2,1.65) rot=(0,0,1;0rad)
FEATURE [Part::Feature] Part__Feature055  label="SOLID055"
  shape: bbox 6 x 8.7 x 1.75 mm, 246 faces (baked)
FEATURE [App::Part] SOIC_14_3_9x8_7mm_P1_27mm  label="SOIC-14_3.9x8.7mm_P1.27mm"
  Group = -> [Part__Feature055]
  Origin = -> Origin110
  Placement = pos=(169.25,-106.75,1.65) rot=(0,0,1;0rad)
FEATURE [Part::Feature] Part__Feature056  label="SOLID056"
  shape: bbox 6 x 8.7 x 1.75 mm, 246 faces (baked)
FEATURE [App::Part] SOIC_14_3_9x8_7mm_P1_27mm001  label="SOIC-14_3.9x8.7mm_P1.27mm001"
  Group = -> [Part__Feature056]
  Origin = -> Origin111
  Placement = pos=(169.7,-137.95,1.65) rot=(0,0,1;0rad)
FEATURE [Part::Feature] Part__Feature057  label="SOLID057"
  shape: bbox 1.6 x 0.8 x 0.45 mm, 26 faces (baked)
FEATURE [App::Part] R_0603_1608Metric012
  Group = -> [Part__Feature057]
  Origin = -> Origin112
  Placement = pos=(213.8,-144.6,1.65) rot=(0,0,1;0rad)
FEATURE [Part::Feature] Part__Feature058  label="SOLID058"
  shape: bbox 1.6 x 0.8 x 0.45 mm, 26 faces (baked)
FEATURE [App::Part] R_0603_1608Metric013
  Group = -> [Part__Feature058]
  Origin = -> Origin113
  Placement = pos=(213.8,-141.8,1.65) rot=(0,0,1;0rad)
FEATURE [Part::Feature] Part__Feature059  label="COMPOUND"
  shape: bbox 140 x 85 x 1.6 mm, 95 faces (baked)
FEATURE [App::Part] Open_CASCADE_STEP_translator_6_9_1  label="Open CASCADE STEP translator 6.9 1"
  Group = -> [ALPS_RS6011SY_Body,ALPS_RS6011SY_Body001,ALPS_RS6011SY_Body002,C_0603_1608Metric,C_0603_1608Metric001,C_0603_1608Metric002,C_0603_1608Metric003,C_0603_1608Metric004,C_0603_1608Metric005,C_0603_1608Metric006,C_0603_1608Metric007,C_0603_1608Metric008,C_0603_1608Metric009,C_0603_1608Metric010,C_0603_1608Metric011,C_0603_1608Metric012,C_0603_1608Metric013,C_0603_1608Metric014,C_0603_1608Metric015,+41 more]
  Origin = -> Origin114
  Placement = pos=(90,115,-1) rot=(0,1,0;3.14159rad)
FEATURE [Sketcher::SketchObject] Sketch011
  ExternalGeometry = -> [Pad007]
  FullyConstrained = true
  MapMode = 5
  Placement = pos=(-2.14e-14,-48.736,1.07e-14) rot=(-0.57735,-0.57735,0.57735;4.18879rad)
  Support = -> [Pad007]
  sketch-geometry (12):
    g0: LineSegment StartX=-15 StartY=-32 StartZ=0 EndX=-9 EndY=-32 EndZ=0
    g1: LineSegment StartX=-9 StartY=-32 StartZ=0 EndX=-9 EndY=-123 EndZ=0
    g2: LineSegment StartX=-9 StartY=-123 StartZ=0 EndX=-15 EndY=-123 EndZ=0
    g3: LineSegment StartX=-15 StartY=-123 StartZ=0 EndX=-15 EndY=-32 EndZ=0
    g4: LineSegment StartX=124 StartY=-32 StartZ=0 EndX=118 EndY=-32 EndZ=0
    g5: LineSegment StartX=118 StartY=-32 StartZ=0 EndX=118 EndY=-123 EndZ=0
    g6: LineSegment StartX=118 StartY=-123 StartZ=0 EndX=124 EndY=-123 EndZ=0
    g7: LineSegment StartX=124 StartY=-123 StartZ=0 EndX=124 EndY=-32 EndZ=0
    g8: LineSegment StartX=-9 StartY=-32 StartZ=0 EndX=-15 EndY=-1.42e-14 EndZ=0
    g9: LineSegment StartX=-9 StartY=-123 StartZ=0 EndX=-15 EndY=-155 EndZ=0
    g10: LineSegment StartX=118 StartY=-123 StartZ=0 EndX=124 EndY=-155 EndZ=0
    g11: LineSegment StartX=118 StartY=-32 StartZ=0 EndX=124 EndY=1.918e-13 EndZ=0
  constraints (32):
    c: Coincident(g0,g1)
    c: Coincident(g1,g2)
    c: Coincident(g2,g3)
    c: Coincident(g3,g0)
    c: Horizontal(g0)
    c: Horizontal(g2)
    c: Vertical(g1)
    c: Vertical(g3)
    c: PointOnObject(g0,g-3)
    c: Coincident(g4,g5)
    c: Coincident(g5,g6)
    c: Coincident(g6,g7)
    c: Coincident(g7,g4)
    c: Horizontal(g4)
    c: Horizontal(g6)
    c: Vertical(g5)
    c: Vertical(g7)
    c: PointOnObject(g4,g-4)
    c: Coincident(g8,g0)
    c: Coincident(g8,g-3)
    c: Coincident(g9,g1)
    c: Coincident(g9,g-3)
    c: Coincident(g10,g5)
    c: Coincident(g10,g-4)
    c: Coincident(g11,g4)
    c: Coincident(g11,g-4)
    c: Equal(g11,g8)
    c: Equal(g8,g9)
    c: Equal(g9,g10)
    c: Equal(g0,g4)
    c: DistanceY(g1,g1) = 91
    c: DistanceX(g0,g0) = 6
FEATURE [PartDesign::Pocket] Pocket007
  BaseFeature = -> Pad007
  Length = 200
  Length2 = 100
  Placement = pos=(0,0,0) rot=(0.57735,0.57735,0.57735;2.0944rad)
  Profile = -> Sketch011
  Type = 0
FEATURE [Sketcher::SketchObject] Sketch012
  ExternalGeometry = -> [Pocket007]
  FullyConstrained = true
  MapMode = 5
  Placement = pos=(0,1.3e-14,9) rot=(0,0,-1;1.5708rad)
  Support = -> [Pocket007]
  sketch-geometry (10):
    g0: LineSegment StartX=-30.264 StartY=-50 StartZ=0 EndX=29.736 EndY=-50 EndZ=0
    g1: LineSegment StartX=29.736 StartY=-50 StartZ=0 EndX=29.736 EndY=-105 EndZ=0
    g2: LineSegment StartX=29.736 StartY=-105 StartZ=0 EndX=-30.264 EndY=-105 EndZ=0
    g3: LineSegment StartX=-30.264 StartY=-105 StartZ=0 EndX=-30.264 EndY=-50 EndZ=0
    g4: LineSegment StartX=-30.264 StartY=-50 StartZ=0 EndX=-52.264 EndY=-32 EndZ=0
    g5: LineSegment StartX=-52.264 StartY=-123 StartZ=0 EndX=-30.264 EndY=-105 EndZ=0
    g6: Circle CenterX=-30.264 CenterY=-50 CenterZ=0 NormalX=0 NormalY=0 NormalZ=1 AngleXU=0 Radius=1.875
    g7: Circle CenterX=29.736 CenterY=-50 CenterZ=0 NormalX=0 NormalY=0 NormalZ=1 AngleXU=0 Radius=1.875
    g8: Circle CenterX=29.736 CenterY=-105 CenterZ=0 NormalX=0 NormalY=0 NormalZ=1 AngleXU=0 Radius=1.875
    g9: Circle CenterX=-30.264 CenterY=-105 CenterZ=0 NormalX=0 NormalY=0 NormalZ=1 AngleXU=0 Radius=1.875
  constraints (24):
    c: Coincident(g0,g1)
    c: Coincident(g1,g2)
    c: Coincident(g2,g3)
    c: Coincident(g3,g0)
    c: Horizontal(g0)
    c: Horizontal(g2)
    c: Vertical(g1)
    c: Vertical(g3)
    c: DistanceX(g-4,g0) = 22
    c: Coincident(g4,g0)
    c: Coincident(g4,g-4)
    c: Coincident(g5,g-4)
    c: Coincident(g5,g2)
    c: Equal(g4,g5)
    c: DistanceY(g3,g3) = 55
    c: DistanceX(g0,g0) = 60
    c: Coincident(g6,g0)
    c: Coincident(g7,g0)
    c: Coincident(g8,g1)
    c: Coincident(g9,g2)
    c: Radius(g6) = 1.875
    c: Equal(g6,g7)
    c: Equal(g6,g8)
    c: Equal(g6,g9)
FEATURE [PartDesign::Pocket] Pocket008
  BaseFeature = -> Pocket007
  Length = 200
  Length2 = 100
  Placement = pos=(0,0,0) rot=(0.57735,0.57735,0.57735;2.0944rad)
  Profile = -> Sketch012
  Type = 0
FEATURE [PartDesign::Plane] DatumPlane001
  Length = 142.65
  MapMode = 5
  Placement = pos=(-8e-16,1.3e-15,3) rot=(0.707107,0.707107,0;3.14159rad)
  ResizeMode = 0
  Support = -> [Pocket008]
  Width = 208.65
FEATURE [Sketcher::SketchObject] Sketch013
  FullyConstrained = false
  MapMode = 5
  Placement = pos=(-8e-16,1.3e-15,3) rot=(0.707107,0.707107,0;3.14159rad)
  Support = -> [DatumPlane001]
  sketch-geometry (10):
    g0: Circle CenterX=34.9044 CenterY=-145.1 CenterZ=0 NormalX=0 NormalY=0 NormalZ=1 AngleXU=0 Radius=3.2
    g1: Circle CenterX=34.9044 CenterY=-145.1 CenterZ=0 NormalX=0 NormalY=0 NormalZ=1 AngleXU=0 Radius=0.1
    g2: Circle CenterX=35.0928 CenterY=-39.9489 CenterZ=0 NormalX=0 NormalY=0 NormalZ=1 AngleXU=0 Radius=0.1
    g3: Circle CenterX=35.0928 CenterY=-39.9489 CenterZ=0 NormalX=0 NormalY=0 NormalZ=1 AngleXU=0 Radius=3.2
    g4: Circle CenterX=-5.04568 CenterY=-79.8989 CenterZ=0 NormalX=0 NormalY=0 NormalZ=1 AngleXU=0 Radius=0.1
    g5: Circle CenterX=-5.04568 CenterY=-79.8989 CenterZ=0 NormalX=0 NormalY=0 NormalZ=1 AngleXU=0 Radius=3.2
    g6: Circle CenterX=-40.1904 CenterY=-145.1 CenterZ=0 NormalX=0 NormalY=0 NormalZ=1 AngleXU=0 Radius=0.1
    g7: Circle CenterX=-40.1904 CenterY=-145.1 CenterZ=0 NormalX=0 NormalY=0 NormalZ=1 AngleXU=0 Radius=3.2
    g8: Circle CenterX=-40.0962 CenterY=-40.1373 CenterZ=0 NormalX=0 NormalY=0 NormalZ=1 AngleXU=0 Radius=0.1
    g9: Circle CenterX=-40.0962 CenterY=-40.1373 CenterZ=0 NormalX=0 NormalY=0 NormalZ=1 AngleXU=0 Radius=3.2
  constraints (15):
    c: Coincident(g1,g0)
    c: Radius(g1) = 0.1
    c: Radius(g0) = 3.2
    c: Coincident(g3,g2)
    c: Coincident(g5,g4)
    c: Coincident(g7,g6)
    c: Coincident(g9,g8)
    c: Equal(g1,g2)
    c: Equal(g2,g4)
    c: Equal(g4,g6)
    c: Equal(g6,g8)
    c: Equal(g0,g3)
    c: Equal(g3,g5)
    c: Equal(g5,g7)
    c: Equal(g7,g9)
FEATURE [PartDesign::Pad] Pad008
  BaseFeature = -> Pocket008
  Direction = (1,1,1)
  Length = 4
  Length2 = 100
  Placement = pos=(0,0,0) rot=(0.57735,0.57735,0.57735;2.0944rad)
  Profile = -> Sketch013
  Type = 0
FEATURE [Sketcher::SketchObject] Sketch014
  ExternalGeometry = -> [Pad008]
  FullyConstrained = false
  MapMode = 5
  Placement = pos=(2.87e-14,65.264,-1.44e-14) rot=(0.57735,0.57735,0.57735;4.18879rad)
  Support = -> [Pad008]
  sketch-geometry (6):
    g0: Circle CenterX=-19 CenterY=-20 CenterZ=0 NormalX=0 NormalY=0 NormalZ=1 AngleXU=0 Radius=5.2
    g1: Circle CenterX=-19 CenterY=-60 CenterZ=0 NormalX=0 NormalY=0 NormalZ=1 AngleXU=0 Radius=5.2
    g2: Circle CenterX=-19 CenterY=-100 CenterZ=0 NormalX=0 NormalY=0 NormalZ=1 AngleXU=0 Radius=5.2
    g3: Circle CenterX=-19 CenterY=-20 CenterZ=0 NormalX=0 NormalY=0 NormalZ=1 AngleXU=0 Radius=2.5
    g4: Circle CenterX=-19 CenterY=-60 CenterZ=0 NormalX=0 NormalY=0 NormalZ=1 AngleXU=0 Radius=2.5
    g5: Circle CenterX=-19 CenterY=-100 CenterZ=0 NormalX=0 NormalY=0 NormalZ=1 AngleXU=0 Radius=2.5
  constraints (10):
    c: Coincident(g0,g-3)
    c: Coincident(g1,g-4)
    c: Coincident(g2,g-5)
    c: Equal(g2,g1)
    c: Equal(g1,g0)
    c: Radius(g0) = 5.2
    c: Coincident(g3,g0)
    c: Equal(g3,g-3)
    c: Coincident(g4,g1)
    c: Coincident(g5,g2)
FEATURE [PartDesign::Pad] Pad009
  BaseFeature = -> Pad008
  Direction = (1,1,1)
  Length = 8
  Length2 = 100
  Placement = pos=(0,0,0) rot=(0.57735,0.57735,0.57735;2.0944rad)
  Profile = -> Sketch014
  Reversed = true
  Type = 0
FEATURE [PartDesign::Plane] DatumPlane002
  Length = 140.066
  MapMode = 5
  Placement = pos=(2e-16,0,0) rot=(0.57735,0.57735,0.57735;2.0944rad)
  ResizeMode = 0
  Support = -> [Pad009]
  Width = 175.066
FEATURE [Sketcher::SketchObject] Sketch015
  AttachmentOffset = pos=(0,0,-4) rot=(0,0,1;0rad)
  ExternalGeometry = -> [Pad009]
  FullyConstrained = false
  MapMode = 5
  Placement = pos=(-4,9e-16,-9e-16) rot=(0.57735,0.57735,0.57735;2.0944rad)
  Support = -> [DatumPlane002]
  sketch-geometry (6):
    g0: LineSegment StartX=58.264 StartY=-56.041 StartZ=0 EndX=61.264 EndY=-97 EndZ=0
    g1: LineSegment StartX=58.264 StartY=-56.041 StartZ=0 EndX=61.264 EndY=-12 EndZ=0
    g2: ArcOfCircle CenterX=-93.433 CenterY=-54.5004 CenterZ=0 NormalX=0 NormalY=0 NormalZ=1 AngleXU=0 Radius=151.705 StartAngle=5.89445 EndAngle=6.67193
    g3: LineSegment StartX=61.264 StartY=-12 StartZ=0 EndX=46.9524 EndY=3 EndZ=0
    g4: LineSegment StartX=61.264 StartY=-97.0017 StartZ=0 EndX=46.9527 EndY=-112 EndZ=0
    g5: LineSegment StartX=61.264 StartY=-12 StartZ=0 EndX=61.264 EndY=-97.0017 EndZ=0
  constraints (10):
    c: PointOnObject(g0,g2)
    c: Coincident(g1,g0)
    c: Coincident(g5,g4)
    c: Vertical(g5)
    c: DistanceX(g0,g3) = 3
    c: Coincident(g3,g5)
    c: Coincident(g3,g1)
    c: Coincident(g3,g-3)
    c: Coincident(g2,g3)
    c: Coincident(g4,g2)
FEATURE [PartDesign::Pad] Pad010
  BaseFeature = -> Pad009
  Direction = (1,1,1)
  Length = 3
  Length2 = 100
  Placement = pos=(0,0,0) rot=(0.57735,0.57735,0.57735;2.0944rad)
  Profile = -> Sketch015
  Reversed = true
  Type = 0
FEATURE [PartDesign::LinearPattern] LinearPattern
  BaseFeature = -> Pad010
  Direction = -> Sketch015 [N_Axis]
  Length = 145
  Occurrences = 3
  Originals = -> [Pad010]
  Placement = pos=(0,0,0) rot=(0.57735,0.57735,0.57735;2.0944rad)
  Reversed = true
FEATURE [PartDesign::Chamfer] Chamfer
  Angle = 45
  Base = -> LinearPattern [Edge10,Edge9,Edge5,Edge7,Edge13]
  BaseFeature = -> LinearPattern
  ChamferType = 1
  FlipDirection = false
  Placement = pos=(0,0,0) rot=(0.57735,0.57735,0.57735;2.0944rad)
  Size = 2
  Size2 = 3.8
  SupportTransform = false
FEATURE [PartDesign::Body] Body001  label="CaseFront"
  Group = -> [Sketch,Pad,Sketch001,Pocket,Sketch002,Pad001,Sketch010,Pad007,Sketch011,Pocket007,Sketch012,Pocket008,DatumPlane001,Sketch013,Pad008,Sketch014,Pad009,DatumPlane002,Sketch015,Pad010,LinearPattern,Chamfer]
  Origin = -> Origin050
  Tip = -> Chamfer
FEATURE [Sketcher::SketchObject] Sketch016
  FullyConstrained = true
  MapMode = 5
  Support = -> [XY_Plane]
  sketch-geometry (8):
    g0: LineSegment StartX=-0.6 StartY=2.05 StartZ=0 EndX=0.6 EndY=2.05 EndZ=0
    g1: LineSegment StartX=0.6 StartY=2.05 StartZ=0 EndX=0.6 EndY=-2.05 EndZ=0
    g2: LineSegment StartX=0.6 StartY=-2.05 StartZ=0 EndX=-0.6 EndY=-2.05 EndZ=0
    g3: LineSegment StartX=-0.6 StartY=-2.05 StartZ=0 EndX=-0.6 EndY=2.05 EndZ=0
    g4: LineSegment StartX=-4 StartY=12.95 StartZ=0 EndX=4 EndY=12.95 EndZ=0
    g5: LineSegment StartX=4 StartY=12.95 StartZ=0 EndX=4 EndY=-5.05 EndZ=0
    g6: LineSegment StartX=4 StartY=-5.05 StartZ=0 EndX=-4 EndY=-5.05 EndZ=0
    g7: LineSegment StartX=-4 StartY=-5.05 StartZ=0 EndX=-4 EndY=12.95 EndZ=0
  constraints (21):
    c: Coincident(g0,g1)
    c: Coincident(g1,g2)
    c: Coincident(g2,g3)
    c: Coincident(g3,g0)
    c: Horizontal(g0)
    c: Vertical(g3)
    c: Symmetric(g2,g1,g-2)
    c: Symmetric(g1,g0,g-1)
    c: DistanceX(g0,g0) = 1.2
    c: DistanceY(g1,g1) = 4.1
    c: Coincident(g4,g5)
    c: Coincident(g5,g6)
    c: Coincident(g6,g7)
    c: Coincident(g7,g4)
    c: Horizontal(g4)
    c: Vertical(g5)
    c: Vertical(g7)
    c: Symmetric(g6,g5,g-2)
    c: DistanceX(g6,g6) = 8
    c: DistanceY(g5,g5) = 18
    c: DistanceY(g5,g1) = 3
FEATURE [PartDesign::Pad] Pad011
  Direction = (1,1,1)
  Length = 10
  Length2 = 100
  Profile = -> Sketch016
  Type = 0
FEATURE [Sketcher::SketchObject] Sketch017
  ExternalGeometry = -> [Pad011]
  FullyConstrained = true
  MapMode = 5
  Placement = pos=(0,12.95,0) rot=(0,0.707107,0.707107;3.14159rad)
  Support = -> [Pad011]
  sketch-geometry (3):
    g0: Circle CenterX=0 CenterY=5 CenterZ=0 NormalX=0 NormalY=0 NormalZ=1 AngleXU=0 Radius=2.5
    g1: LineSegment StartX=0 StartY=5 StartZ=0 EndX=0 EndY=10 EndZ=0
    g2: LineSegment StartX=0 StartY=5 StartZ=0 EndX=0 EndY=0 EndZ=0
  constraints (8):
    c: PointOnObject(g0,g-2)
    c: Radius(g0) = 2.5
    c: Coincident(g1,g0)
    c: PointOnObject(g1,g-3)
    c: Vertical(g1)
    c: Coincident(g2,g0)
    c: Coincident(g2,g-1)
    c: Equal(g1,g2)
FEATURE [PartDesign::Pocket] Pocket009
  BaseFeature = -> Pad011
  Length = 8
  Length2 = 100
  Profile = -> Sketch017
  Type = 0
FEATURE [PartDesign::Fillet] Fillet001
  Base = -> Pocket009 [Edge9,Edge15,Edge8,Edge7]
  BaseFeature = -> Pocket009
  Radius = 1
  SupportTransform = false
FEATURE [PartDesign::Chamfer] Chamfer001
  Angle = 45
  Base = -> Fillet001 [Edge20,Edge21,Edge22,Edge19]
  BaseFeature = -> Fillet001
  ChamferType = 0
  FlipDirection = false
  Size = 0.3
  Size2 = 1
  SupportTransform = false
FEATURE [PartDesign::Chamfer] Chamfer002
  Angle = 45
  Base = -> Chamfer001 [Edge39,Edge35,Edge38,Edge41]
  BaseFeature = -> Chamfer001
  ChamferType = 0
  FlipDirection = false
  Size = 0.3
  Size2 = 1
  SupportTransform = false
FEATURE [PartDesign::Body] Body005  label="LinearPotScrewAdapter"
  Group = -> [Sketch016,Pad011,Sketch017,Pocket009,Fillet001,Chamfer001,Chamfer002]
  Origin = -> Origin
  Tip = -> Chamfer002
FEATURE [Sketcher::SketchObject] Sketch018
  FullyConstrained = false
  MapMode = 5
  Placement = pos=(0,0,0) rot=(0.57735,0.57735,0.57735;2.0944rad)
  Support = -> [YZ_Plane115]
  sketch-geometry (12):
    g0: LineSegment StartX=-48.7324 StartY=3.00118 StartZ=0 EndX=-48.7324 EndY=15.0012 EndZ=0
    g1: LineSegment StartX=-48.7324 StartY=15.0012 StartZ=0 EndX=46.4535 EndY=15.0012 EndZ=0
    g2: LineSegment StartX=46.4535 StartY=15.0012 StartZ=0 EndX=64.8216 EndY=-4.01607 EndZ=0
    g3: LineSegment StartX=64.8216 StartY=-4.01607 StartZ=0 EndX=64.8216 EndY=-104.752 EndZ=0
    g4: LineSegment StartX=64.8216 StartY=-104.752 StartZ=0 EndX=46.2314 EndY=-123.999 EndZ=0
    g5: LineSegment StartX=46.2314 StartY=-123.999 StartZ=0 EndX=-48.7324 EndY=-123.999 EndZ=0
    g6: LineSegment StartX=-48.7324 StartY=-123.999 StartZ=0 EndX=-48.7324 EndY=-111.999 EndZ=0
    g7: LineSegment StartX=-48.7324 StartY=-111.999 StartZ=0 EndX=46.2314 EndY=-111.999 EndZ=0
    g8: LineSegment StartX=46.2314 StartY=-111.999 StartZ=0 EndX=60.9582 EndY=-96.7516 EndZ=0
    g9: LineSegment StartX=60.9582 StartY=-96.7516 StartZ=0 EndX=60.9582 EndY=-12.0161 EndZ=0
    g10: LineSegment StartX=60.9582 StartY=-12.0161 StartZ=0 EndX=46.4535 EndY=3.00118 EndZ=0
    g11: LineSegment StartX=46.4535 StartY=3.00118 StartZ=0 EndX=-48.7324 EndY=3.00118 EndZ=0
  constraints (30):
    c: Vertical(g0)
    c: Coincident(g1,g0)
    c: Horizontal(g1)
    c: Coincident(g2,g1)
    c: Coincident(g4,g3)
    c: Coincident(g5,g4)
    c: Horizontal(g5)
    c: Coincident(g6,g5)
    c: Vertical(g6)
    c: Coincident(g7,g6)
    c: Horizontal(g7)
    c: Coincident(g8,g7)
    c: Coincident(g10,g9)
    c: Coincident(g11,g10)
    c: Coincident(g11,g0)
    c: Horizontal(g11)
    c: Equal(g0,g6)
    c: Parallel(g10,g2)
    c: Parallel(g8,g4)
    c: Equal(g11,g1)
    c: Equal(g7,g5)
    c: DistanceX(g6,g0) = 0
    c: DistanceY(g6,g0) = 115
    c: DistanceY(g9,g2) = 8
    c: DistanceY(g3,g8) = 8
    c: DistanceY(g6,g6) = 12
    c: Coincident(g2,g3)
    c: Vertical(g3)
    c: Vertical(g9)
    c: Coincident(g8,g9)
FEATURE [PartDesign::Pad] Pad012
  Direction = (1,1,1)
  Length = 155
  Length2 = 100
  Placement = pos=(0,0,0) rot=(0.57735,0.57735,0.57735;2.0944rad)
  Profile = -> Sketch018
  Reversed = true
  Type = 0
FEATURE [PartDesign::Plane] DatumPlane003
  Length = 181.752
  MapMode = 5
  Placement = pos=(2.88e-14,64.8216,-2.16e-14) rot=(0.57735,0.57735,0.57735;4.18879rad)
  ResizeMode = 0
  Support = -> [Pad012]
  Width = 212.753
FEATURE [Sketcher::SketchObject] Sketch019
  FullyConstrained = false
  MapMode = 5
  Placement = pos=(2.88e-14,64.8216,-2.16e-14) rot=(0.57735,0.57735,0.57735;4.18879rad)
  Support = -> [DatumPlane003]
  sketch-geometry (19):
    g0: Circle CenterX=-19 CenterY=-20 CenterZ=0 NormalX=0 NormalY=0 NormalZ=1 AngleXU=0 Radius=2.5
    g1: Circle CenterX=-19 CenterY=-60 CenterZ=0 NormalX=0 NormalY=0 NormalZ=1 AngleXU=0 Radius=2.5
    g2: Circle CenterX=-19 CenterY=-100 CenterZ=0 NormalX=0 NormalY=0 NormalZ=1 AngleXU=0 Radius=2.5
    g3: Circle CenterX=-47.1476 CenterY=-60 CenterZ=0 NormalX=0 NormalY=0 NormalZ=1 AngleXU=0 Radius=3.5
    g4: Circle CenterX=-47.1476 CenterY=-90 CenterZ=0 NormalX=0 NormalY=0 NormalZ=1 AngleXU=0 Radius=3.5
    g5: Circle CenterX=-84.2562 CenterY=-90 CenterZ=0 NormalX=0 NormalY=0 NormalZ=1 AngleXU=0 Radius=3.5
    g6: Circle CenterX=-84.2562 CenterY=-60 CenterZ=0 NormalX=0 NormalY=0 NormalZ=1 AngleXU=0 Radius=3.5
    g7: LineSegment StartX=-35 StartY=-10 StartZ=0 EndX=-111.8 EndY=-10 EndZ=0
    g8: LineSegment StartX=-111.8 StartY=-10 StartZ=0 EndX=-111.8 EndY=-22 EndZ=0
    g9: LineSegment StartX=-111.8 StartY=-22 StartZ=0 EndX=-35 EndY=-22 EndZ=0
    g10: LineSegment StartX=-35 StartY=-22 StartZ=0 EndX=-35 EndY=-10 EndZ=0
    g11: LineSegment StartX=-84 StartY=-134.96 StartZ=0 EndX=-24 EndY=-134.96 EndZ=0
    g12: LineSegment StartX=-24 StartY=-134.96 StartZ=0 EndX=-24 EndY=-123.667 EndZ=0
    g13: LineSegment StartX=-84 StartY=-134.96 StartZ=0 EndX=-84 EndY=-129.76 EndZ=0
    g14: LineSegment StartX=-84 StartY=-129.76 StartZ=0 EndX=-68.641 EndY=-129.76 EndZ=0
    g15: LineSegment StartX=-68.641 StartY=-129.76 StartZ=0 EndX=-68.641 EndY=-126.713 EndZ=0
    g16: LineSegment StartX=-68.641 StartY=-126.713 StartZ=0 EndX=-53.2819 EndY=-126.713 EndZ=0
    g17: LineSegment StartX=-53.2819 StartY=-126.713 StartZ=0 EndX=-53.2819 EndY=-123.667 EndZ=0
    g18: LineSegment StartX=-53.2819 StartY=-123.667 StartZ=0 EndX=-24 EndY=-123.667 EndZ=0
  constraints (52):
    c: Equal(g0,g1)
    c: Equal(g1,g2)
    c: DistanceX(g1,g0) = 0
    c: DistanceX(g2,g1) = 0
    c: DistanceX(g0,g-1) = 19
    c: DistanceY(g0,g-1) = 20
    c: DistanceY(g1,g0) = 40
    c: DistanceY(g2,g1) = 40
    c: DistanceY(g4,g3) = 30
    c: DistanceX(g4,g3) = 0
    c: DistanceY(g5,g6) = 30
    c: DistanceX(g6,g5) = 0
    c: Coincident(g7,g8)
    c: Coincident(g8,g9)
    c: Coincident(g9,g10)
    c: Coincident(g10,g7)
    c: Horizontal(g7)
    c: Horizontal(g9)
    c: Vertical(g8)
    c: Vertical(g10)
    c: DistanceY(g10,g10) = 12
    c: DistanceY(g7,g-1) = 10
    c: DistanceX(g7,g-1) = 35
    c: DistanceX(g7,g7) = 76.8
    c: DistanceY(g1,g3) = 0
    c: DistanceY(g6,g3) = 0
    c: Radius(g0) = 2.5
    c: Equal(g3,g4)
    c: Equal(g3,g6)
    c: Equal(g6,g5)
    c: Radius(g3) = 3.5
    c: Horizontal(g11)
    c: Coincident(g12,g11)
    c: Vertical(g12)
    c: Coincident(g13,g11)
    c: Vertical(g13)
    c: Coincident(g14,g13)
    c: Horizontal(g14)
    c: Coincident(g15,g14)
    c: Coincident(g16,g15)
    c: Horizontal(g16)
    c: Coincident(g17,g16)
    c: Vertical(g17)
    c: Coincident(g18,g17)
    c: Coincident(g18,g12)
    c: Horizontal(g18)
    c: Vertical(g15)
    c: Equal(g14,g16)
    c: Equal(g15,g17)
    c: DistanceY(g13,g13) = 5.2
    c: DistanceX(g11,g-1) = 24
    c: DistanceX(g11,g11) = 60
FEATURE [PartDesign::Pocket] Pocket010
  BaseFeature = -> Pad012
  Length = 20
  Length2 = 100
  Placement = pos=(0,0,0) rot=(0.57735,0.57735,0.57735;2.0944rad)
  Profile = -> Sketch019
  Type = 0
FEATURE [PartDesign::Plane] DatumPlane004
  Length = 181.752
  MapMode = 5
  Placement = pos=(-2.16e-14,-48.7324,3.25e-14) rot=(0.57735,0.57735,-0.57735;2.0944rad)
  ResizeMode = 0
  Support = -> [Pocket010]
  Width = 212.753
FEATURE [Sketcher::SketchObject] Sketch020
  FullyConstrained = false
  MapMode = 5
  Placement = pos=(-2.16e-14,-48.7324,3.25e-14) rot=(-0.57735,-0.57735,0.57735;4.18879rad)
  Support = -> [DatumPlane004]
  sketch-geometry (8):
    g0: LineSegment StartX=-15.9669 StartY=-31.8239 StartZ=0 EndX=-9.00004 EndY=-31.8239 EndZ=0
    g1: LineSegment StartX=-9.00004 StartY=-31.8239 StartZ=0 EndX=-9.00004 EndY=-123.158 EndZ=0
    g2: LineSegment StartX=-9.00004 StartY=-123.158 StartZ=0 EndX=-15.9669 EndY=-123.158 EndZ=0
    g3: LineSegment StartX=-15.9669 StartY=-123.158 StartZ=0 EndX=-15.9669 EndY=-31.8239 EndZ=0
    g4: LineSegment StartX=117.959 StartY=-31.8239 StartZ=0 EndX=125.587 EndY=-31.8239 EndZ=0
    g5: LineSegment StartX=125.587 StartY=-31.8239 StartZ=0 EndX=125.587 EndY=-123.158 EndZ=0
    g6: LineSegment StartX=125.587 StartY=-123.158 StartZ=0 EndX=117.959 EndY=-123.158 EndZ=0
    g7: LineSegment StartX=117.959 StartY=-123.158 StartZ=0 EndX=117.959 EndY=-31.8239 EndZ=0
  constraints (18):
    c: Coincident(g0,g1)
    c: Coincident(g1,g2)
    c: Coincident(g2,g3)
    c: Coincident(g3,g0)
    c: Horizontal(g0)
    c: Horizontal(g2)
    c: Vertical(g1)
    c: Vertical(g3)
    c: Coincident(g4,g5)
    c: Coincident(g5,g6)
    c: Coincident(g6,g7)
    c: Coincident(g7,g4)
    c: Horizontal(g4)
    c: Horizontal(g6)
    c: Vertical(g5)
    c: Vertical(g7)
    c: DistanceY(g1,g6) = 0
    c: Equal(g1,g7)
FEATURE [PartDesign::Pocket] Pocket011
  BaseFeature = -> Pocket010
  Length = 300
  Length2 = 100
  Placement = pos=(0,0,0) rot=(0.57735,0.57735,0.57735;2.0944rad)
  Profile = -> Sketch020
  Type = 0
FEATURE [PartDesign::Plane] DatumPlane005
  Length = 142.147
  MapMode = 5
  Placement = pos=(-1e-15,7e-15,9.00004) rot=(0,0,-1;1.5708rad)
  ResizeMode = 0
  Support = -> [Pocket011]
  Width = 208.594
FEATURE [Sketcher::SketchObject] Sketch021
  FullyConstrained = false
  MapMode = 5
  Placement = pos=(-1e-15,7e-15,9.00004) rot=(0,0,-1;1.5708rad)
  Support = -> [DatumPlane005]
  sketch-geometry (8):
    g0: LineSegment StartX=-30.2682 StartY=-50.0119 StartZ=0 EndX=29.7318 EndY=-50.0119 EndZ=0
    g1: LineSegment StartX=29.7318 StartY=-50.0119 StartZ=0 EndX=29.7318 EndY=-105.012 EndZ=0
    g2: LineSegment StartX=29.7318 StartY=-105.012 StartZ=0 EndX=-30.2682 EndY=-105.012 EndZ=0
    g3: LineSegment StartX=-30.2682 StartY=-105.012 StartZ=0 EndX=-30.2682 EndY=-50.0119 EndZ=0
    g4: Circle CenterX=-30.2682 CenterY=-50.0119 CenterZ=0 NormalX=0 NormalY=0 NormalZ=1 AngleXU=0 Radius=1.91
    g5: Circle CenterX=29.7318 CenterY=-50.0119 CenterZ=0 NormalX=0 NormalY=0 NormalZ=1 AngleXU=0 Radius=1.91
    g6: Circle CenterX=-30.2682 CenterY=-105.012 CenterZ=0 NormalX=0 NormalY=0 NormalZ=1 AngleXU=0 Radius=1.91
    g7: Circle CenterX=29.7318 CenterY=-105.012 CenterZ=0 NormalX=0 NormalY=0 NormalZ=1 AngleXU=0 Radius=1.91
  constraints (18):
    c: Coincident(g0,g1)
    c: Coincident(g1,g2)
    c: Coincident(g2,g3)
    c: Coincident(g3,g0)
    c: Horizontal(g0)
    c: Horizontal(g2)
    c: Vertical(g1)
    c: Vertical(g3)
    c: DistanceY(g3,g3) = 55
    c: DistanceX(g0,g0) = 60
    c: Coincident(g4,g0)
    c: Coincident(g5,g0)
    c: Coincident(g6,g2)
    c: Coincident(g7,g1)
    c: Radius(g7) = 1.91
    c: Equal(g7,g6)
    c: Equal(g6,g4)
    c: Equal(g4,g5)
FEATURE [PartDesign::Pocket] Pocket012
  BaseFeature = -> Pocket011
  Length = 400
  Length2 = 100
  Placement = pos=(0,0,0) rot=(0.57735,0.57735,0.57735;2.0944rad)
  Profile = -> Sketch021
  Type = 0
FEATURE [PartDesign::Plane] DatumPlane006
  Length = 139.569
  MapMode = 5
  Placement = pos=(-155,1.721e-13,-1.033e-13) rot=(-0.57735,-0.57735,0.57735;2.0944rad)
  ResizeMode = 0
  Support = -> [Pocket012]
  Width = 175.014
FEATURE [Sketcher::SketchObject] Sketch022
  AttachmentOffset = pos=(0,0,-3) rot=(0,0,1;0rad)
  FullyConstrained = false
  MapMode = 5
  Placement = pos=(-152,1.698e-13,-1.009e-13) rot=(0.57735,0.57735,-0.57735;4.18879rad)
  Support = -> [DatumPlane006]
  sketch-geometry (6):
    g0: LineSegment StartX=42 StartY=115.992 StartZ=0 EndX=45.594 EndY=115.992 EndZ=0
    g1: LineSegment StartX=45.594 StartY=115.992 StartZ=0 EndX=62.7427 EndY=98.8963 EndZ=0
    g2: LineSegment StartX=62.7427 StartY=98.8963 StartZ=0 EndX=62.7427 EndY=9.07643 EndZ=0
    g3: LineSegment StartX=62.7427 StartY=9.07643 StartZ=0 EndX=47.0133 EndY=-5.11201 EndZ=0
    g4: LineSegment StartX=47.0133 StartY=-5.11201 StartZ=0 EndX=42 EndY=-5.11201 EndZ=0
    g5: LineSegment StartX=42 StartY=115.992 StartZ=0 EndX=42 EndY=-5.11201 EndZ=0
  constraints (10):
    c: Horizontal(g0)
    c: Coincident(g1,g0)
    c: Coincident(g2,g1)
    c: Vertical(g2)
    c: Horizontal(g4)
    c: DistanceX(g-1,g0) = 42
    c: Coincident(g4,g3)
    c: Vertical(g5)
    c: Coincident(g4,g5)
    c: Coincident(g0,g5)
FEATURE [PartDesign::Pad] Pad013
  BaseFeature = -> Pocket012
  Direction = (1,1,1)
  Length = 3
  Length2 = 100
  Placement = pos=(0,0,0) rot=(0.57735,0.57735,0.57735;2.0944rad)
  Profile = -> Sketch022
  Reversed = true
  Type = 0
FEATURE [PartDesign::Plane] DatumPlane007
  Length = 139.569
  MapMode = 5
  Placement = pos=(-155,1.721e-13,-1.033e-13) rot=(0.57735,0.57735,-0.57735;4.18879rad)
  ResizeMode = 0
  Support = -> [DatumPlane006]
  Width = 175.014
FEATURE [PartDesign::Plane] DatumPlane008
  Length = 139.569
  MapMode = 5
  Placement = pos=(3.57e-14,0,0) rot=(0.57735,0.57735,0.57735;2.0944rad)
  ResizeMode = 0
  Support = -> [Pad013]
  Width = 175.014
FEATURE [Sketcher::SketchObject] Sketch023
  AttachmentOffset = pos=(0,0,-3) rot=(0,0,1;0rad)
  FullyConstrained = false
  MapMode = 5
  Placement = pos=(-3,4e-15,-2.7e-15) rot=(0.57735,0.57735,0.57735;2.0944rad)
  Support = -> [DatumPlane008]
  sketch-geometry (6):
    g0: LineSegment StartX=42 StartY=7.3262 StartZ=0 EndX=42 EndY=-117.652 EndZ=0
    g1: LineSegment StartX=42 StartY=-117.652 StartZ=0 EndX=46.047 EndY=-117.652 EndZ=0
    g2: LineSegment StartX=46.047 StartY=-117.652 StartZ=0 EndX=62.613 EndY=-100.248 EndZ=0
    g3: LineSegment StartX=62.613 StartY=-100.248 StartZ=0 EndX=62.613 EndY=-9.44945 EndZ=0
    g4: LineSegment StartX=62.613 StartY=-9.44945 StartZ=0 EndX=47.0955 EndY=6.69712 EndZ=0
    g5: LineSegment StartX=47.0955 StartY=6.69712 StartZ=0 EndX=42 EndY=7.3262 EndZ=0
  constraints (10):
    c: Vertical(g0)
    c: Coincident(g1,g0)
    c: Horizontal(g1)
    c: Coincident(g2,g1)
    c: Coincident(g3,g2)
    c: Vertical(g3)
    c: Coincident(g4,g3)
    c: Coincident(g5,g4)
    c: Coincident(g5,g0)
    c: DistanceX(g-1,g0) = 42
FEATURE [PartDesign::Pad] Pad014
  BaseFeature = -> Pad013
  Direction = (1,1,1)
  Length = 3
  Length2 = 100
  Placement = pos=(0,0,0) rot=(0.57735,0.57735,0.57735;2.0944rad)
  Profile = -> Sketch023
  Reversed = true
  Type = 0
FEATURE [Sketcher::SketchObject] Sketch024
  FullyConstrained = false
  MapMode = 5
  Placement = pos=(3.57e-14,0,0) rot=(0.57735,0.57735,0.57735;2.0944rad)
  Support = -> [DatumPlane008]
  sketch-geometry (21):
    g0: LineSegment StartX=53.4841 StartY=-22.5 StartZ=0 EndX=57.4841 EndY=-22.5 EndZ=0
    g1: LineSegment StartX=57.4841 StartY=-22.5 StartZ=0 EndX=57.4841 EndY=-33.9028 EndZ=0
    g2: LineSegment StartX=57.4841 StartY=-33.9028 StartZ=0 EndX=53.4841 EndY=-33.9028 EndZ=0
    g3: LineSegment StartX=53.4841 StartY=-33.9028 StartZ=0 EndX=53.4841 EndY=-22.5 EndZ=0
    g4: LineSegment StartX=53.4841 StartY=-49.1341 StartZ=0 EndX=57.4841 EndY=-49.1341 EndZ=0
    g5: LineSegment StartX=57.4841 StartY=-49.1341 StartZ=0 EndX=57.4841 EndY=-60.5369 EndZ=0
    g6: LineSegment StartX=57.4841 StartY=-60.5369 StartZ=0 EndX=53.4841 EndY=-60.5369 EndZ=0
    g7: LineSegment StartX=53.4841 StartY=-60.5369 StartZ=0 EndX=53.4841 EndY=-49.1341 EndZ=0
    g8: LineSegment StartX=53.4841 StartY=-75.7682 StartZ=0 EndX=57.4841 EndY=-75.7682 EndZ=0
    g9: LineSegment StartX=57.4841 StartY=-75.7682 StartZ=0 EndX=57.4841 EndY=-87.171 EndZ=0
    g10: LineSegment StartX=57.4841 StartY=-87.171 StartZ=0 EndX=53.4841 EndY=-87.171 EndZ=0
    g11: LineSegment StartX=53.4841 StartY=-87.171 StartZ=0 EndX=53.4841 EndY=-75.7682 EndZ=0
    g12: LineSegment StartX=53.4841 StartY=-75.7682 StartZ=0 EndX=53.4841 EndY=-60.5369 EndZ=0
    g13: LineSegment StartX=53.4841 StartY=-49.1341 StartZ=0 EndX=53.4841 EndY=-33.9028 EndZ=0
    g14: LineSegment StartX=53.4841 StartY=-22.5 StartZ=0 EndX=53.4841 EndY=0 EndZ=0
    g15: LineSegment StartX=0 StartY=14.2771 StartZ=0 EndX=46.6354 EndY=14.2771 EndZ=0
    g16: LineSegment StartX=46.6354 StartY=14.2771 StartZ=0 EndX=46.6354 EndY=-123.948 EndZ=0
    g17: LineSegment StartX=46.6354 StartY=-123.948 StartZ=0 EndX=0 EndY=-123.948 EndZ=0
    g18: LineSegment StartX=0 StartY=-123.948 StartZ=0 EndX=0 EndY=14.2771 EndZ=0
    g19: LineSegment StartX=46.6354 StartY=-123.948 StartZ=0 EndX=53.4841 EndY=-87.171 EndZ=0
    g20: LineSegment StartX=53.4841 StartY=-22.5 StartZ=0 EndX=46.6354 EndY=14.2771 EndZ=0
  constraints (54):
    c: Coincident(g0,g1)
    c: Coincident(g1,g2)
    c: Coincident(g2,g3)
    c: Coincident(g3,g0)
    c: Horizontal(g0)
    c: Horizontal(g2)
    c: Vertical(g1)
    c: Vertical(g3)
    c: Coincident(g4,g5)
    c: Coincident(g5,g6)
    c: Coincident(g6,g7)
    c: Coincident(g7,g4)
    c: Horizontal(g4)
    c: Horizontal(g6)
    c: Vertical(g5)
    c: Vertical(g7)
    c: Coincident(g8,g9)
    c: Coincident(g9,g10)
    c: Coincident(g10,g11)
    c: Coincident(g11,g8)
    c: Horizontal(g8)
    c: Horizontal(g10)
    c: Vertical(g9)
    c: Vertical(g11)
    c: Equal(g0,g4)
    c: Equal(g4,g8)
    c: Equal(g7,g3)
    c: Equal(g3,g11)
    c: Coincident(g12,g8)
    c: Coincident(g12,g6)
    c: Coincident(g13,g4)
    c: Coincident(g13,g2)
    c: Vertical(g13)
    c: Vertical(g12)
    c: Equal(g12,g13)
    c: Coincident(g14,g0)
    c: PointOnObject(g14,g-1)
    c: Vertical(g14)
    c: DistanceY(g14,g14) = 22.5
    c: Coincident(g15,g16)
    c: Coincident(g16,g17)
    c: Coincident(g17,g18)
    c: Coincident(g18,g15)
    c: Horizontal(g15)
    c: Horizontal(g17)
    c: Vertical(g16)
    c: Vertical(g18)
    c: PointOnObject(g15,g-2)
    c: Coincident(g19,g16)
    c: Coincident(g19,g10)
    c: Coincident(g20,g0)
    c: Coincident(g20,g15)
    c: Equal(g20,g19)
    c: DistanceX(g2,g2) = 4
FEATURE [PartDesign::Pocket] Pocket013
  BaseFeature = -> Pad014
  Length = 300
  Length2 = 100
  Placement = pos=(0,0,0) rot=(0.57735,0.57735,0.57735;2.0944rad)
  Profile = -> Sketch024
  Type = 0
FEATURE [PartDesign::Plane] DatumPlane009
  Length = 181.752
  MapMode = 5
  Placement = pos=(2.71e-14,60.9582,-1.421e-13) rot=(0.57735,0.57735,-0.57735;2.0944rad)
  ResizeMode = 0
  Support = -> [Pocket013]
  Width = 212.753
FEATURE [Sketcher::SketchObject] Sketch025
  FullyConstrained = false
  MapMode = 5
  Placement = pos=(2.71e-14,60.9582,-1.421e-13) rot=(0.57735,0.57735,-0.57735;2.0944rad)
  Support = -> [DatumPlane009]
  sketch-geometry (34):
    g0: LineSegment StartX=19.4022 StartY=-135 StartZ=0 EndX=90.2547 EndY=-135 EndZ=0
    g1: LineSegment StartX=90.2547 StartY=-135 StartZ=0 EndX=90.2547 EndY=-143 EndZ=0
    g2: LineSegment StartX=90.2547 StartY=-143 StartZ=0 EndX=19.4022 EndY=-143 EndZ=0
    g3: LineSegment StartX=19.4022 StartY=-143 StartZ=0 EndX=19.4022 EndY=-135 EndZ=0
    g4: LineSegment StartX=27.6096 StartY=-137.5 StartZ=0 EndX=39.6096 EndY=-137.5 EndZ=0
    g5: LineSegment StartX=39.6096 StartY=-137.5 StartZ=0 EndX=39.6096 EndY=-140.5 EndZ=0
    g6: LineSegment StartX=39.6096 StartY=-140.5 StartZ=0 EndX=27.6096 EndY=-140.5 EndZ=0
    g7: LineSegment StartX=27.6096 StartY=-140.5 StartZ=0 EndX=27.6096 EndY=-137.5 EndZ=0
    g8: LineSegment StartX=70.0473 StartY=-137.5 StartZ=0 EndX=82.0473 EndY=-137.5 EndZ=0
    g9: LineSegment StartX=82.0473 StartY=-137.5 StartZ=0 EndX=82.0473 EndY=-140.5 EndZ=0
    g10: LineSegment StartX=82.0473 StartY=-140.5 StartZ=0 EndX=70.0473 EndY=-140.5 EndZ=0
    g11: LineSegment StartX=70.0473 StartY=-140.5 StartZ=0 EndX=70.0473 EndY=-137.5 EndZ=0
    g12: LineSegment StartX=39.6096 StartY=-140.5 StartZ=0 EndX=70.0473 EndY=-140.5 EndZ=0
    g13: LineSegment StartX=27.6096 StartY=-137.5 StartZ=0 EndX=19.4022 EndY=-135 EndZ=0
    g14: LineSegment StartX=27.6096 StartY=-140.5 StartZ=0 EndX=19.4022 EndY=-143 EndZ=0
    g15: LineSegment StartX=82.0473 StartY=-140.5 StartZ=0 EndX=90.2547 EndY=-143 EndZ=0
    g16: LineSegment StartX=82.0473 StartY=-137.5 StartZ=0 EndX=90.2547 EndY=-135 EndZ=0
    g17: LineSegment StartX=46.6978 StartY=-31.3875 StartZ=0 EndX=96.8695 EndY=-31.3875 EndZ=0
    g18: LineSegment StartX=96.8695 StartY=-31.3875 StartZ=0 EndX=96.8695 EndY=-39.3875 EndZ=0
    g19: LineSegment StartX=96.8695 StartY=-39.3875 StartZ=0 EndX=46.6978 EndY=-39.3875 EndZ=0
    g20: LineSegment StartX=46.6978 StartY=-39.3875 StartZ=0 EndX=46.6978 EndY=-31.3875 EndZ=0
    g21: LineSegment StartX=52.5765 StartY=-33.8875 StartZ=0 EndX=64.5765 EndY=-33.8875 EndZ=0
    g22: LineSegment StartX=64.5765 StartY=-33.8875 StartZ=0 EndX=64.5765 EndY=-36.8875 EndZ=0
    g23: LineSegment StartX=64.5765 StartY=-36.8875 StartZ=0 EndX=52.5765 EndY=-36.8875 EndZ=0
    g24: LineSegment StartX=52.5765 StartY=-36.8875 StartZ=0 EndX=52.5765 EndY=-33.8875 EndZ=0
    g25: LineSegment StartX=78.9908 StartY=-33.8875 StartZ=0 EndX=90.9908 EndY=-33.8875 EndZ=0
    g26: LineSegment StartX=90.9908 StartY=-33.8875 StartZ=0 EndX=90.9908 EndY=-36.8875 EndZ=0
    g27: LineSegment StartX=90.9908 StartY=-36.8875 StartZ=0 EndX=78.9908 EndY=-36.8875 EndZ=0
    g28: LineSegment StartX=78.9908 StartY=-36.8875 StartZ=0 EndX=78.9908 EndY=-33.8875 EndZ=0
    g29: LineSegment StartX=64.5765 StartY=-36.8875 StartZ=0 EndX=78.9908 EndY=-36.8875 EndZ=0
    g30: LineSegment StartX=52.5765 StartY=-33.8875 StartZ=0 EndX=46.6978 EndY=-31.3875 EndZ=0
    g31: LineSegment StartX=52.5765 StartY=-36.8875 StartZ=0 EndX=46.6978 EndY=-39.3875 EndZ=0
    g32: LineSegment StartX=90.9908 StartY=-36.8875 StartZ=0 EndX=96.8695 EndY=-39.3875 EndZ=0
    g33: LineSegment StartX=90.9908 StartY=-33.8875 StartZ=0 EndX=96.8695 EndY=-31.3875 EndZ=0
  constraints (85):
    c: Coincident(g0,g1)
    c: Coincident(g1,g2)
    c: Coincident(g2,g3)
    c: Coincident(g3,g0)
    c: Horizontal(g0)
    c: Horizontal(g2)
    c: Vertical(g1)
    c: Vertical(g3)
    c: DistanceY(g3,g3) = 8
    c: DistanceY(g0,g-1) = 135
    c: Coincident(g4,g5)
    c: Coincident(g5,g6)
    c: Coincident(g6,g7)
    c: Coincident(g7,g4)
    c: Horizontal(g4)
    c: Horizontal(g6)
    c: Vertical(g5)
    c: Vertical(g7)
    c: Coincident(g8,g9)
    c: Coincident(g9,g10)
    c: Coincident(g10,g11)
    c: Coincident(g11,g8)
    c: Horizontal(g8)
    c: Horizontal(g10)
    c: Vertical(g9)
    c: Vertical(g11)
    c: Coincident(g12,g5)
    c: Coincident(g12,g10)
    c: Horizontal(g12)
    c: Equal(g11,g5)
    c: Equal(g4,g8)
    c: Coincident(g13,g4)
    c: Coincident(g13,g0)
    c: Coincident(g14,g6)
    c: Coincident(g14,g2)
    c: Coincident(g15,g9)
    c: Coincident(g15,g1)
    c: Coincident(g16,g8)
    c: Coincident(g16,g0)
    c: Equal(g16,g15)
    c: Equal(g15,g14)
    c: DistanceX(g4,g4) = 12
    c: DistanceY(g7,g7) = 3
    c: Coincident(g17,g18)
    c: Coincident(g18,g19)
    c: Coincident(g19,g20)
    c: Coincident(g20,g17)
    c: Horizontal(g17)
    c: Horizontal(g19)
    c: Vertical(g18)
    c: Vertical(g20)
    c: DistanceY(g20,g20) = 8
    c: Coincident(g21,g22)
    c: Coincident(g22,g23)
    c: Coincident(g23,g24)
    c: Coincident(g24,g21)
    c: Horizontal(g21)
    c: Horizontal(g23)
    c: Vertical(g22)
    c: Vertical(g24)
    c: Coincident(g25,g26)
    c: Coincident(g26,g27)
    c: Coincident(g27,g28)
    c: Coincident(g28,g25)
    c: Horizontal(g25)
    c: Horizontal(g27)
    c: Vertical(g26)
    c: Vertical(g28)
    c: Equal(g25,g21)
    c: Equal(g21,g4)
    c: Equal(g24,g7)
    c: Equal(g24,g28)
    c: Coincident(g29,g22)
    c: Coincident(g29,g27)
    c: Horizontal(g29)
    c: Coincident(g30,g21)
    c: Coincident(g30,g17)
    c: Coincident(g31,g23)
    c: Coincident(g31,g19)
    c: Coincident(g32,g26)
    c: Coincident(g32,g18)
    c: Coincident(g33,g25)
    c: Coincident(g33,g17)
    c: Equal(g30,g31)
    c: Equal(g31,g32)
FEATURE [PartDesign::Pocket] Pocket014
  BaseFeature = -> Pocket013
  Length = 2
  Length2 = 100
  Placement = pos=(0,0,0) rot=(0.57735,0.57735,0.57735;2.0944rad)
  Profile = -> Sketch025
  Type = 0
FEATURE [Sketcher::SketchObject] Sketch026
  FullyConstrained = false
  MapMode = 5
  Placement = pos=(2.71e-14,60.9582,-1.421e-13) rot=(0.57735,0.57735,-0.57735;2.0944rad)
  Support = -> [DatumPlane009]
  sketch-geometry (4):
    g0: LineSegment StartX=32.9475 StartY=-40.2319 StartZ=0 EndX=94.2332 EndY=-40.2319 EndZ=0
    g1: LineSegment StartX=94.2332 StartY=-40.2319 StartZ=0 EndX=94.2332 EndY=-113.747 EndZ=0
    g2: LineSegment StartX=94.2332 StartY=-113.747 StartZ=0 EndX=32.9475 EndY=-113.747 EndZ=0
    g3: LineSegment StartX=32.9475 StartY=-113.747 StartZ=0 EndX=32.9475 EndY=-40.2319 EndZ=0
  constraints (8):
    c: Coincident(g0,g1)
    c: Coincident(g1,g2)
    c: Coincident(g2,g3)
    c: Coincident(g3,g0)
    c: Horizontal(g0)
    c: Horizontal(g2)
    c: Vertical(g1)
    c: Vertical(g3)
FEATURE [PartDesign::Pocket] Pocket015
  BaseFeature = -> Pocket014
  Length = 1
  Length2 = 100
  Placement = pos=(0,0,0) rot=(0.57735,0.57735,0.57735;2.0944rad)
  Profile = -> Sketch026
  Type = 0
FEATURE [Sketcher::SketchObject] Sketch027
  ExternalGeometry = -> [Pocket015]
  FullyConstrained = false
  MapMode = 5
  Placement = pos=(2.71e-14,60.9582,-1.421e-13) rot=(0.57735,0.57735,-0.57735;2.0944rad)
  Support = -> [DatumPlane009]
  sketch-geometry (6):
    g0: Circle CenterX=19 CenterY=-20 CenterZ=0 NormalX=0 NormalY=0 NormalZ=1 AngleXU=0 Radius=4.5
    g1: Circle CenterX=19 CenterY=-20 CenterZ=0 NormalX=0 NormalY=0 NormalZ=1 AngleXU=0 Radius=2.5
    g2: Circle CenterX=19 CenterY=-60 CenterZ=0 NormalX=0 NormalY=0 NormalZ=1 AngleXU=0 Radius=4.5
    g3: Circle CenterX=19 CenterY=-60 CenterZ=0 NormalX=0 NormalY=0 NormalZ=1 AngleXU=0 Radius=2.5
    g4: Circle CenterX=19 CenterY=-100 CenterZ=0 NormalX=0 NormalY=0 NormalZ=1 AngleXU=0 Radius=4.5
    g5: Circle CenterX=19 CenterY=-100 CenterZ=0 NormalX=0 NormalY=0 NormalZ=1 AngleXU=0 Radius=2.5
  constraints (9):
    c: Coincident(g0,g-3)
    c: Coincident(g1,g0)
    c: Coincident(g2,g-4)
    c: Coincident(g3,g2)
    c: Coincident(g4,g-5)
    c: Coincident(g5,g4)
    c: Equal(g4,g2)
    c: Equal(g2,g0)
    c: Radius(g0) = 4.5
FEATURE [PartDesign::Pad] Pad015
  BaseFeature = -> Pocket015
  Direction = (1,1,1)
  Length = 7
  Length2 = 100
  Placement = pos=(0,0,0) rot=(0.57735,0.57735,0.57735;2.0944rad)
  Profile = -> Sketch027
  Type = 0
FEATURE [Sketcher::SketchObject] Sketch028
  FullyConstrained = true
  MapMode = 5
  Placement = pos=(-2.16e-14,-48.7324,3.25e-14) rot=(-0.57735,-0.57735,0.57735;4.18879rad)
  Support = -> [DatumPlane004]
  sketch-geometry (20):
    g0: LineSegment StartX=0 StartY=-12.5 StartZ=0 EndX=109 EndY=-12.5 EndZ=0
    g1: LineSegment StartX=109 StartY=-12.5 StartZ=0 EndX=109 EndY=-142.5 EndZ=0
    g2: LineSegment StartX=109 StartY=-142.5 StartZ=0 EndX=0 EndY=-142.5 EndZ=0
    g3: LineSegment StartX=0 StartY=-142.5 StartZ=0 EndX=0 EndY=-12.5 EndZ=0
    g4: LineSegment StartX=0 StartY=-12.5 StartZ=0 EndX=-10 EndY=-12.5 EndZ=0
    g5: LineSegment StartX=-10 StartY=-12.5 StartZ=0 EndX=-10 EndY=-22.5 EndZ=0
    g6: LineSegment StartX=-10 StartY=-22.5 StartZ=0 EndX=0 EndY=-22.5 EndZ=0
    g7: LineSegment StartX=0 StartY=-22.5 StartZ=0 EndX=0 EndY=-12.5 EndZ=0
    g8: LineSegment StartX=109 StartY=-12.5 StartZ=0 EndX=119 EndY=-12.5 EndZ=0
    g9: LineSegment StartX=119 StartY=-12.5 StartZ=0 EndX=119 EndY=-22.5 EndZ=0
    g10: LineSegment StartX=119 StartY=-22.5 StartZ=0 EndX=109 EndY=-22.5 EndZ=0
    g11: LineSegment StartX=109 StartY=-22.5 StartZ=0 EndX=109 EndY=-12.5 EndZ=0
    g12: LineSegment StartX=0 StartY=-142.5 StartZ=0 EndX=-10 EndY=-142.5 EndZ=0
    g13: LineSegment StartX=-10 StartY=-142.5 StartZ=0 EndX=-10 EndY=-132.5 EndZ=0
    g14: LineSegment StartX=-10 StartY=-132.5 StartZ=0 EndX=0 EndY=-132.5 EndZ=0
    g15: LineSegment StartX=0 StartY=-132.5 StartZ=0 EndX=0 EndY=-142.5 EndZ=0
    g16: LineSegment StartX=109 StartY=-142.5 StartZ=0 EndX=119 EndY=-142.5 EndZ=0
    g17: LineSegment StartX=119 StartY=-142.5 StartZ=0 EndX=119 EndY=-132.5 EndZ=0
    g18: LineSegment StartX=119 StartY=-132.5 StartZ=0 EndX=109 EndY=-132.5 EndZ=0
    g19: LineSegment StartX=109 StartY=-132.5 StartZ=0 EndX=109 EndY=-142.5 EndZ=0
  constraints (56):
    c: Coincident(g0,g1)
    c: Coincident(g1,g2)
    c: Coincident(g2,g3)
    c: Coincident(g3,g0)
    c: Horizontal(g0)
    c: Horizontal(g2)
    c: Vertical(g1)
    c: Vertical(g3)
    c: PointOnObject(g0,g-2)
    c: DistanceX(g0,g0) = 109
    c: DistanceY(g3,g3) = 130
    c: DistanceY(g0,g-1) = 12.5
    c: Coincident(g4,g5)
    c: Coincident(g5,g6)
    c: Coincident(g6,g7)
    c: Coincident(g7,g4)
    c: Horizontal(g4)
    c: Horizontal(g6)
    c: Vertical(g5)
    c: Vertical(g7)
    c: Coincident(g4,g0)
    c: Equal(g6,g7)
    c: Coincident(g8,g9)
    c: Coincident(g9,g10)
    c: Coincident(g10,g11)
    c: Coincident(g11,g8)
    c: Horizontal(g8)
    c: Horizontal(g10)
    c: Vertical(g9)
    c: Vertical(g11)
    c: Coincident(g8,g0)
    c: Equal(g10,g9)
    c: Coincident(g12,g13)
    c: Coincident(g13,g14)
    c: Coincident(g14,g15)
    c: Coincident(g15,g12)
    c: Horizontal(g12)
    c: Horizontal(g14)
    c: Vertical(g13)
    c: Vertical(g15)
    c: Coincident(g12,g2)
    c: Coincident(g16,g17)
    c: Coincident(g17,g18)
    c: Coincident(g18,g19)
    c: Coincident(g19,g16)
    c: Horizontal(g16)
    c: Horizontal(g18)
    c: Vertical(g17)
    c: Vertical(g19)
    c: Coincident(g16,g1)
    c: Equal(g16,g17)
    c: Equal(g17,g12)
    c: Equal(g12,g13)
    c: Equal(g13,g10)
    c: Equal(g10,g6)
    c: DistanceY(g5,g5) = 10
FEATURE [PartDesign::Pocket] Pocket016
  BaseFeature = -> Pad015
  Length = 2
  Length2 = 100
  Placement = pos=(0,0,0) rot=(0.57735,0.57735,0.57735;2.0944rad)
  Profile = -> Sketch028
  Type = 0
FEATURE [PartDesign::ShapeBinder] CopyPocket016
  Placement = pos=(-155,4.13e-13,-2.323e-13) rot=(0,0,1;0rad)
  TraceSupport = false
FEATURE [PartDesign::Plane] DatumPlane010
  Length = 139.569
  MapMode = 5
  Placement = pos=(-155,4.13e-13,-2.323e-13) rot=(-0.57735,0.57735,0.57735;4.18879rad)
  ResizeMode = 0
  Support = -> [CopyPocket016]
  Width = 175.014
FEATURE [Sketcher::SketchObject] Sketch029
  AttachmentOffset = pos=(0,0,-13.5) rot=(0,0,1;0rad)
  FullyConstrained = false
  MapMode = 5
  Placement = pos=(-141.5,3.92e-13,-1.963e-13) rot=(-0.57735,0.57735,0.57735;4.18879rad)
  Support = -> [DatumPlane010]
  sketch-geometry (9):
    g0: LineSegment StartX=-60.7105 StartY=-22.5092 StartZ=0 EndX=-60.7105 EndY=-87.5092 EndZ=0
    g1: LineSegment StartX=-60.7105 StartY=-22.5092 StartZ=0 EndX=7.1e-15 EndY=-33.2141 EndZ=0
    g2: LineSegment StartX=-60.7105 StartY=-87.5092 StartZ=0 EndX=-7.1e-15 EndY=-76.8043 EndZ=0
    g3: ArcOfCircle CenterX=-3.84306 CenterY=-55.0092 CenterZ=0 NormalX=0 NormalY=0 NormalZ=1 AngleXU=0 Radius=22.1313 StartAngle=4.88692 EndAngle=7.67945
    g4: LineSegment StartX=-60.7105 StartY=-22.5092 StartZ=0 EndX=-60.7105 EndY=-53.3774 EndZ=0
    g5: LineSegment StartX=-3.84306 StartY=-55.0092 StartZ=0 EndX=-60.7105 EndY=-55.0092 EndZ=0
    g6: LineSegment StartX=-3.84306 StartY=-55.0092 StartZ=0 EndX=5.00109 EndY=-55.0092 EndZ=0
    g7: Circle CenterX=5.00109 CenterY=-55.0092 CenterZ=0 NormalX=0 NormalY=0 NormalZ=1 AngleXU=0 Radius=3.5
    g8: Circle CenterX=-39.9989 CenterY=-55.0092 CenterZ=0 NormalX=0 NormalY=0 NormalZ=1 AngleXU=0 Radius=2.45
  constraints (22):
    c: Vertical(g0)
    c: DistanceY(g0,g0) = 65
    c: Coincident(g1,g0)
    c: PointOnObject(g1,g-2)
    c: Coincident(g2,g0)
    c: PointOnObject(g2,g-2)
    c: Coincident(g3,g2)
    c: Angle(g0,g1) = 1.39626
    c: Angle(g2,g0) = 1.39626
    c: Tangent(g3,g1) = 1.5708
    c: Coincident(g4,g0)
    c: PointOnObject(g4,g0)
    c: Coincident(g5,g3)
    c: PointOnObject(g5,g0)
    c: Horizontal(g5)
    c: Coincident(g6,g3)
    c: Horizontal(g6)
    c: Coincident(g7,g6)
    c: Radius(g7) = 3.5
    c: PointOnObject(g8,g5)
    c: Radius(g8) = 2.45
    c: DistanceX(g8,g7) = 45
FEATURE [PartDesign::Pad] Pad016
  Direction = (1,1,1)
  Length = 5
  Length2 = 100
  Placement = pos=(-155,4.13e-13,-2.323e-13) rot=(-0.57735,0.57735,0.57735;4.18879rad)
  Profile = -> Sketch029
  Reversed = true
  Type = 0
FEATURE [Sketcher::SketchObject] Sketch030
  FullyConstrained = true
  MapMode = 5
  Placement = pos=(-141.5,3.937e-13,-1.961e-13) rot=(-0.57735,0.57735,0.57735;4.18879rad)
  Support = -> [Pad016]
FEATURE [Sketcher::SketchObject] Sketch031
  ExternalGeometry = -> [Pad016]
  FullyConstrained = false
  MapMode = 5
  Placement = pos=(-141.5,3.937e-13,-1.961e-13) rot=(-0.57735,0.57735,0.57735;4.18879rad)
  Support = -> [Pad016]
  sketch-geometry (6):
    g0: LineSegment StartX=-7.1e-15 StartY=-76.8043 StartZ=0 EndX=-40.6542 EndY=-66.048 EndZ=0
    g1: LineSegment StartX=-40.692 StartY=-43.8266 StartZ=0 EndX=7.1e-15 EndY=-33.2141 EndZ=0
    g2: ArcOfCircle CenterX=-35.7256 CenterY=-54.9289 CenterZ=0 NormalX=0 NormalY=0 NormalZ=1 AngleXU=0 Radius=12.1625 StartAngle=1.99143 EndAngle=4.29516
    g3: LineSegment StartX=7.1e-15 StartY=-33.2141 StartZ=0 EndX=-60.7105 EndY=-22.5092 EndZ=0
    g4: LineSegment StartX=-60.7105 StartY=-22.5092 StartZ=0 EndX=-60.7105 EndY=-87.5092 EndZ=0
    g5: LineSegment StartX=-60.7105 StartY=-87.5092 StartZ=0 EndX=-7.1e-15 EndY=-76.8043 EndZ=0
  constraints (11):
    c: Coincident(g0,g-4)
    c: Coincident(g1,g-5)
    c: Equal(g0,g1)
    c: Coincident(g2,g0)
    c: Coincident(g2,g1)
    c: Coincident(g3,g1)
    c: Coincident(g3,g-5)
    c: Coincident(g4,g3)
    c: Coincident(g4,g-4)
    c: Coincident(g5,g4)
    c: Coincident(g5,g0)
FEATURE [PartDesign::Pad] Pad017
  BaseFeature = -> Pad016
  Direction = (1,1,1)
  Length = 3
  Length2 = 100
  Placement = pos=(-155,4.13e-13,-2.323e-13) rot=(-0.57735,0.57735,0.57735;4.18879rad)
  Profile = -> Sketch031
  Type = 0
FEATURE [Sketcher::SketchObject] Sketch032
  ExternalGeometry = -> [Pad017]
  FullyConstrained = false
  MapMode = 5
  Placement = pos=(-141.5,3.967e-13,-1.999e-13) rot=(-0.57735,0.57735,0.57735;4.18879rad)
  Support = -> [Pad017]
  sketch-geometry (1):
    g0: Circle CenterX=5.00109 CenterY=-55.0092 CenterZ=0 NormalX=0 NormalY=0 NormalZ=1 AngleXU=0 Radius=21.115
  constraints (1):
    c: Coincident(g-3,g0)
FEATURE [PartDesign::Pocket] Pocket017
  BaseFeature = -> Pad017
  Length = 1
  Length2 = 100
  Placement = pos=(-155,4.13e-13,-2.323e-13) rot=(-0.57735,0.57735,0.57735;4.18879rad)
  Profile = -> Sketch032
  Type = 0
FEATURE [Sketcher::SketchObject] Sketch033
  FullyConstrained = false
  MapMode = 5
  Placement = pos=(-155,60.7105,-4.042e-13) rot=(-0.57735,0.57735,0.57735;2.0944rad)
  Support = -> [Pocket017]
  sketch-geometry (8):
    g0: LineSegment StartX=27.88 StartY=-14.7324 StartZ=0 EndX=39.4381 EndY=-14.7324 EndZ=0
    g1: LineSegment StartX=39.4381 StartY=-14.7324 StartZ=0 EndX=39.4381 EndY=-17.2587 EndZ=0
    g2: LineSegment StartX=39.4381 StartY=-17.2587 StartZ=0 EndX=27.88 EndY=-17.2587 EndZ=0
    g3: LineSegment StartX=27.88 StartY=-17.2587 StartZ=0 EndX=27.88 EndY=-14.7324 EndZ=0
    g4: LineSegment StartX=70.323 StartY=-14.7324 StartZ=0 EndX=81.818 EndY=-14.7324 EndZ=0
    g5: LineSegment StartX=81.818 StartY=-14.7324 StartZ=0 EndX=81.818 EndY=-17.2587 EndZ=0
    g6: LineSegment StartX=81.818 StartY=-17.2587 StartZ=0 EndX=70.323 EndY=-17.2587 EndZ=0
    g7: LineSegment StartX=70.323 StartY=-17.2587 StartZ=0 EndX=70.323 EndY=-14.7324 EndZ=0
  constraints (16):
    c: Coincident(g0,g1)
    c: Coincident(g1,g2)
    c: Coincident(g2,g3)
    c: Coincident(g3,g0)
    c: Horizontal(g0)
    c: Horizontal(g2)
    c: Vertical(g1)
    c: Vertical(g3)
    c: Coincident(g4,g5)
    c: Coincident(g5,g6)
    c: Coincident(g6,g7)
    c: Coincident(g7,g4)
    c: Horizontal(g4)
    c: Horizontal(g6)
    c: Vertical(g5)
    c: Vertical(g7)
FEATURE [PartDesign::Pad] Pad018
  BaseFeature = -> Pocket017
  Direction = (1,1,1)
  Length = 1.8
  Length2 = 100
  Placement = pos=(-155,4.13e-13,-2.323e-13) rot=(-0.57735,0.57735,0.57735;4.18879rad)
  Profile = -> Sketch033
  Type = 0
FEATURE [Sketcher::SketchObject] Sketch034
  ExternalGeometry = -> [Pad018]
  FullyConstrained = true
  MapMode = 5
  Placement = pos=(-140.5,3.999e-13,-2.066e-13) rot=(-0.57735,0.57735,0.57735;4.18879rad)
  Support = -> [Pad018]
  sketch-geometry (5):
    g0: Circle CenterX=5.00109 CenterY=-55.0092 CenterZ=0 NormalX=0 NormalY=0 NormalZ=1 AngleXU=0 Radius=8.5
    g1: LineSegment StartX=-3.4065 StartY=-53.7592 StartZ=0 EndX=-2.1065 EndY=-53.7592 EndZ=0
    g2: LineSegment StartX=-2.1065 StartY=-53.7592 StartZ=0 EndX=-2.1065 EndY=-56.2592 EndZ=0
    g3: LineSegment StartX=-2.1065 StartY=-56.2592 StartZ=0 EndX=-3.4065 EndY=-56.2592 EndZ=0
    g4: LineSegment StartX=-3.4065 StartY=-56.2592 StartZ=0 EndX=-3.4065 EndY=-53.7592 EndZ=0
  constraints (14):
    c: Coincident(g0,g-3)
    c: Radius(g0) = 8.5
    c: Coincident(g1,g2)
    c: Coincident(g2,g3)
    c: Coincident(g3,g4)
    c: Coincident(g4,g1)
    c: Horizontal(g1)
    c: Horizontal(g3)
    c: Vertical(g2)
    c: Vertical(g4)
    c: PointOnObject(g1,g0)
    c: PointOnObject(g3,g0)
    c: DistanceY(g4,g4) = 2.5
    c: DistanceX(g3,g3) = 1.3
FEATURE [PartDesign::Pocket] Pocket018
  BaseFeature = -> Pad018
  Length = 1
  Length2 = 100
  Placement = pos=(-155,4.13e-13,-2.323e-13) rot=(-0.57735,0.57735,0.57735;4.18879rad)
  Profile = -> Sketch034
  Type = 0
FEATURE [PartDesign::ShapeBinder] CopyPocket016001
  TraceSupport = false
FEATURE [PartDesign::Plane] DatumPlane011
  Length = 139.569
  MapMode = 5
  Placement = pos=(0,0,0) rot=(0.57735,0.57735,0.57735;2.0944rad)
  ResizeMode = 0
  Support = -> [CopyPocket016001]
  Width = 175.014
FEATURE [Sketcher::SketchObject] Sketch035
  AttachmentOffset = pos=(0,0,-30) rot=(0,0,1;0rad)
  FullyConstrained = false
  MapMode = 5
  Placement = pos=(-30,4.66e-14,-7.99e-14) rot=(0.57735,0.57735,0.57735;2.0944rad)
  Support = -> [DatumPlane011]
  sketch-geometry (7):
    g0: LineSegment StartX=60.8632 StartY=-45.7261 StartZ=0 EndX=60.8632 EndY=-94.7552 EndZ=0
    g1: LineSegment StartX=60.8632 StartY=-94.7552 StartZ=0 EndX=1.18502 EndY=-84.2323 EndZ=0
    g2: LineSegment StartX=60.8632 StartY=-45.7261 StartZ=0 EndX=1.18502 EndY=-56.249 EndZ=0
    g3: ArcOfCircle CenterX=3.65213 CenterY=-70.2406 CenterZ=0 NormalX=0 NormalY=0 NormalZ=1 AngleXU=0 Radius=14.2075 StartAngle=1.74533 EndAngle=4.53786
    g4: LineSegment StartX=3.65213 StartY=-70.2406 StartZ=0 EndX=60.8632 EndY=-70.2406 EndZ=0
    g5: Circle CenterX=34.8632 CenterY=-70.2406 CenterZ=0 NormalX=0 NormalY=0 NormalZ=1 AngleXU=0 Radius=2.475
    g6: Circle CenterX=4.86319 CenterY=-70.2406 CenterZ=0 NormalX=0 NormalY=0 NormalZ=1 AngleXU=0 Radius=3.4
  constraints (17):
    c: Vertical(g0)
    c: Coincident(g1,g0)
    c: Coincident(g2,g0)
    c: Coincident(g3,g1)
    c: Angle(g2,g0) = 1.39626
    c: Angle(g0,g1) = 1.39626
    c: Tangent(g3,g2) = -1.5708
    c: Equal(g1,g2)
    c: Coincident(g4,g3)
    c: PointOnObject(g4,g0)
    c: Horizontal(g4)
    c: PointOnObject(g5,g4)
    c: Radius(g5) = 2.475
    c: DistanceX(g6,g5) = 30
    c: DistanceX(g5,g4) = 26
    c: PointOnObject(g6,g4)
    c: Radius(g6) = 3.4
FEATURE [PartDesign::Pad] Pad019
  Direction = (1,1,1)
  Length = 7
  Length2 = 100
  Placement = pos=(0,0,0) rot=(0.57735,0.57735,0.57735;2.0944rad)
  Profile = -> Sketch035
  Reversed = true
  Type = 0
FEATURE [Sketcher::SketchObject] Sketch036
  FullyConstrained = false
  MapMode = 5
  Placement = pos=(1.014e-13,60.8632,-1.554e-13) rot=(0.57735,0.57735,0.57735;4.18879rad)
  Support = -> [Pad019]
  sketch-geometry (8):
    g0: LineSegment StartX=-90.9007 StartY=-33.9526 StartZ=0 EndX=-79.0302 EndY=-33.9526 EndZ=0
    g1: LineSegment StartX=-79.0302 StartY=-33.9526 StartZ=0 EndX=-79.0302 EndY=-36.8061 EndZ=0
    g2: LineSegment StartX=-79.0302 StartY=-36.8061 StartZ=0 EndX=-90.9007 EndY=-36.8061 EndZ=0
    g3: LineSegment StartX=-90.9007 StartY=-36.8061 StartZ=0 EndX=-90.9007 EndY=-33.9526 EndZ=0
    g4: LineSegment StartX=-64.3984 StartY=-34.0636 StartZ=0 EndX=-52.671 EndY=-34.0636 EndZ=0
    g5: LineSegment StartX=-52.671 StartY=-34.0636 StartZ=0 EndX=-52.671 EndY=-36.7732 EndZ=0
    g6: LineSegment StartX=-52.671 StartY=-36.7732 StartZ=0 EndX=-64.3984 EndY=-36.7732 EndZ=0
    g7: LineSegment StartX=-64.3984 StartY=-36.7732 StartZ=0 EndX=-64.3984 EndY=-34.0636 EndZ=0
  constraints (16):
    c: Coincident(g0,g1)
    c: Coincident(g1,g2)
    c: Coincident(g2,g3)
    c: Coincident(g3,g0)
    c: Horizontal(g0)
    c: Horizontal(g2)
    c: Vertical(g1)
    c: Vertical(g3)
    c: Coincident(g4,g5)
    c: Coincident(g5,g6)
    c: Coincident(g6,g7)
    c: Coincident(g7,g4)
    c: Horizontal(g4)
    c: Horizontal(g6)
    c: Vertical(g5)
    c: Vertical(g7)
FEATURE [PartDesign::Pad] Pad020
  BaseFeature = -> Pad019
  Direction = (1,1,1)
  Length = 1.8
  Length2 = 100
  Placement = pos=(0,0,0) rot=(0.57735,0.57735,0.57735;2.0944rad)
  Profile = -> Sketch036
  Type = 0
FEATURE [Sketcher::SketchObject] Sketch037
  ExternalGeometry = -> [Pad020]
  FullyConstrained = false
  MapMode = 5
  Placement = pos=(-37,6.55e-14,-1.033e-13) rot=(0.57735,0.57735,-0.57735;4.18879rad)
  Support = -> [Pad020]
  sketch-geometry (1):
    g0: Circle CenterX=4.86319 CenterY=70.2406 CenterZ=0 NormalX=0 NormalY=0 NormalZ=1 AngleXU=0 Radius=16.1879
  constraints (1):
    c: Coincident(g0,g-3)
FEATURE [PartDesign::Pocket] Pocket019
  BaseFeature = -> Pad020
  Length = 3
  Length2 = 100
  Placement = pos=(0,0,0) rot=(0.57735,0.57735,0.57735;2.0944rad)
  Profile = -> Sketch037
  Type = 0
FEATURE [Sketcher::SketchObject] Sketch038
  ExternalGeometry = -> [Pocket019]
  FullyConstrained = true
  MapMode = 5
  Placement = pos=(-34,6.84e-14,-9.67e-14) rot=(0.57735,0.57735,-0.57735;4.18879rad)
  Support = -> [Pocket019]
  sketch-geometry (5):
    g0: Circle CenterX=4.86319 CenterY=70.2406 CenterZ=0 NormalX=0 NormalY=0 NormalZ=1 AngleXU=0 Radius=8.5
    g1: LineSegment StartX=3.61319 StartY=61.8331 StartZ=0 EndX=6.11319 EndY=61.8331 EndZ=0
    g2: LineSegment StartX=6.11319 StartY=61.8331 StartZ=0 EndX=6.11319 EndY=63.0831 EndZ=0
    g3: LineSegment StartX=6.11319 StartY=63.0831 StartZ=0 EndX=3.61319 EndY=63.0831 EndZ=0
    g4: LineSegment StartX=3.61319 StartY=63.0831 StartZ=0 EndX=3.61319 EndY=61.8331 EndZ=0
  constraints (14):
    c: Coincident(g0,g-3)
    c: Radius(g0) = 8.5
    c: Coincident(g1,g2)
    c: Coincident(g2,g3)
    c: Coincident(g3,g4)
    c: Coincident(g4,g1)
    c: Horizontal(g1)
    c: Horizontal(g3)
    c: Vertical(g2)
    c: Vertical(g4)
    c: PointOnObject(g1,g0)
    c: PointOnObject(g1,g0)
    c: DistanceX(g1,g1) = 2.5
    c: DistanceY(g4,g4) = 1.25
FEATURE [PartDesign::Pocket] Pocket020
  BaseFeature = -> Pocket019
  Length = 1
  Length2 = 100
  Placement = pos=(0,0,0) rot=(0.57735,0.57735,0.57735;2.0944rad)
  Profile = -> Sketch038
  Type = 0
FEATURE [PartDesign::Plane] DatumPlane012
  Length = 142.147
  MapMode = 5
  Placement = pos=(-1.12e-14,5e-15,3.00118) rot=(0.707107,0.707107,0;3.14159rad)
  ResizeMode = 0
  Support = -> [Pocket016]
  Width = 208.594
FEATURE [Sketcher::SketchObject] Sketch039
  FullyConstrained = false
  MapMode = 5
  Placement = pos=(-1.12e-14,5e-15,3.00118) rot=(0.707107,0.707107,0;3.14159rad)
  Support = -> [DatumPlane012]
  sketch-geometry (17):
    g0: LineSegment StartX=-44.2079 StartY=-36.0053 StartZ=0 EndX=52.9468 EndY=-36.0053 EndZ=0
    g1: LineSegment StartX=52.9468 StartY=-36.0053 StartZ=0 EndX=52.9468 EndY=-43.6746 EndZ=0
    g2: LineSegment StartX=52.9468 StartY=-43.6746 StartZ=0 EndX=-44.2079 EndY=-43.6746 EndZ=0
    g3: LineSegment StartX=-44.2079 StartY=-43.6746 StartZ=0 EndX=-44.2079 EndY=-36.0053 EndZ=0
    g4: LineSegment StartX=-8.92645 StartY=-76.2876 StartZ=0 EndX=53.2027 EndY=-76.2876 EndZ=0
    g5: LineSegment StartX=53.2027 StartY=-76.2876 StartZ=0 EndX=53.2027 EndY=-83.9569 EndZ=0
    g6: LineSegment StartX=53.2027 StartY=-83.9569 StartZ=0 EndX=-8.92645 EndY=-83.9569 EndZ=0
    g7: LineSegment StartX=-8.92645 StartY=-83.9569 StartZ=0 EndX=-8.92645 EndY=-76.2876 EndZ=0
    g8: LineSegment StartX=-44.4639 StartY=-141.125 StartZ=0 EndX=53.4838 EndY=-141.125 EndZ=0
    g9: LineSegment StartX=53.4838 StartY=-141.125 StartZ=0 EndX=53.4838 EndY=-148.795 EndZ=0
    g10: LineSegment StartX=53.4838 StartY=-148.795 StartZ=0 EndX=-44.4639 EndY=-148.795 EndZ=0
    g11: LineSegment StartX=-44.4639 StartY=-148.795 StartZ=0 EndX=-44.4639 EndY=-141.125 EndZ=0
    g12: Circle CenterX=-40.0031 CenterY=-39.9623 CenterZ=0 NormalX=0 NormalY=0 NormalZ=1 AngleXU=0 Radius=0.85
    g13: Circle CenterX=35.0151 CenterY=-39.9891 CenterZ=0 NormalX=0 NormalY=0 NormalZ=1 AngleXU=0 Radius=0.85
    g14: Circle CenterX=-4.99393 CenterY=-80.0038 CenterZ=0 NormalX=0 NormalY=0 NormalZ=1 AngleXU=0 Radius=0.85
    g15: Circle CenterX=35.0047 CenterY=-144.992 CenterZ=0 NormalX=0 NormalY=0 NormalZ=1 AngleXU=0 Radius=0.85
    g16: Circle CenterX=-40.0014 CenterY=-144.979 CenterZ=0 NormalX=0 NormalY=0 NormalZ=1 AngleXU=0 Radius=0.85
  constraints (31):
    c: Coincident(g0,g1)
    c: Coincident(g1,g2)
    c: Coincident(g2,g3)
    c: Coincident(g3,g0)
    c: Horizontal(g0)
    c: Horizontal(g2)
    c: Vertical(g1)
    c: Vertical(g3)
    c: Coincident(g4,g5)
    c: Coincident(g5,g6)
    c: Coincident(g6,g7)
    c: Coincident(g7,g4)
    c: Horizontal(g4)
    c: Horizontal(g6)
    c: Vertical(g5)
    c: Vertical(g7)
    c: Coincident(g8,g9)
    c: Coincident(g9,g10)
    c: Coincident(g10,g11)
    c: Coincident(g11,g8)
    c: Horizontal(g8)
    c: Horizontal(g10)
    c: Vertical(g9)
    c: Vertical(g11)
    c: Radius(g15) = 0.85
    c: Equal(g15,g16)
    c: Equal(g16,g14)
    c: Equal(g14,g12)
    c: Equal(g12,g13)
    c: Equal(g11,g3)
    c: Equal(g3,g7)
FEATURE [PartDesign::Pad] Pad021
  BaseFeature = -> Pocket016
  Direction = (1,1,1)
  Length = 3.5
  Length2 = 100
  Placement = pos=(0,0,0) rot=(0.57735,0.57735,0.57735;2.0944rad)
  Profile = -> Sketch039
  Type = 0
FEATURE [PartDesign::Plane] DatumPlane013
  Length = 142.147
  MapMode = 5
  Placement = pos=(-1.12e-14,5e-15,3.00118) rot=(0.707107,0.707107,0;3.14159rad)
  ResizeMode = 0
  Support = -> [DatumPlane012]
  Width = 208.594
FEATURE [PartDesign::Plane] DatumPlane014
  Length = 142.147
  MapMode = 5
  Placement = pos=(2e-15,-9e-16,-0.49882) rot=(0.707107,0.707107,0;3.14159rad)
  ResizeMode = 0
  Support = -> [Pad021]
  Width = 208.594
FEATURE [Sketcher::SketchObject] Sketch040
  FullyConstrained = false
  MapMode = 5
  Placement = pos=(2e-15,-9e-16,-0.49882) rot=(0.707107,0.707107,0;3.14159rad)
  Support = -> [DatumPlane014]
  sketch-geometry (12):
    g0: LineSegment StartX=-34.1949 StartY=-34.3579 StartZ=0 EndX=29.9777 EndY=-34.3579 EndZ=0
    g1: LineSegment StartX=29.9777 StartY=-34.3579 StartZ=0 EndX=29.9777 EndY=-46.7784 EndZ=0
    g2: LineSegment StartX=29.9777 StartY=-46.7784 StartZ=0 EndX=-34.1949 EndY=-46.7784 EndZ=0
    g3: LineSegment StartX=-34.1949 StartY=-46.7784 StartZ=0 EndX=-34.1949 EndY=-34.3579 EndZ=0
    g4: LineSegment StartX=0 StartY=-73.8275 StartZ=0 EndX=39.3621 EndY=-73.8275 EndZ=0
    g5: LineSegment StartX=39.3621 StartY=-73.8275 StartZ=0 EndX=39.3621 EndY=-85.972 EndZ=0
    g6: LineSegment StartX=39.3621 StartY=-85.972 StartZ=0 EndX=0 EndY=-85.972 EndZ=0
    g7: LineSegment StartX=0 StartY=-85.972 StartZ=0 EndX=0 EndY=-73.8275 EndZ=0
    g8: LineSegment StartX=-35.0191 StartY=-139.444 StartZ=0 EndX=30.5336 EndY=-139.444 EndZ=0
    g9: LineSegment StartX=30.5336 StartY=-139.444 StartZ=0 EndX=30.5336 EndY=-150.347 EndZ=0
    g10: LineSegment StartX=30.5336 StartY=-150.347 StartZ=0 EndX=-35.0191 EndY=-150.347 EndZ=0
    g11: LineSegment StartX=-35.0191 StartY=-150.347 StartZ=0 EndX=-35.0191 EndY=-139.444 EndZ=0
  constraints (25):
    c: Coincident(g0,g1)
    c: Coincident(g1,g2)
    c: Coincident(g2,g3)
    c: Coincident(g3,g0)
    c: Horizontal(g0)
    c: Horizontal(g2)
    c: Vertical(g1)
    c: Vertical(g3)
    c: Coincident(g4,g5)
    c: Coincident(g5,g6)
    c: Coincident(g6,g7)
    c: Coincident(g7,g4)
    c: Horizontal(g4)
    c: Horizontal(g6)
    c: Vertical(g5)
    c: Vertical(g7)
    c: PointOnObject(g4,g-2)
    c: Coincident(g8,g9)
    c: Coincident(g9,g10)
    c: Coincident(g10,g11)
    c: Coincident(g11,g8)
    c: Horizontal(g8)
    c: Horizontal(g10)
    c: Vertical(g9)
    c: Vertical(g11)
FEATURE [PartDesign::Pocket] Pocket021
  BaseFeature = -> Pad021
  Length = 1
  Length2 = 100
  Placement = pos=(0,0,0) rot=(0.57735,0.57735,0.57735;2.0944rad)
  Profile = -> Sketch040
  Type = 0
FEATURE [PartDesign::Chamfer] Chamfer003
  Angle = 45
  Base = -> Pocket021 [Edge389,Edge393,Edge385]
  BaseFeature = -> Pocket021
  ChamferType = 1
  FlipDirection = false
  Placement = pos=(0,0,0) rot=(0.57735,0.57735,0.57735;2.0944rad)
  Size = 0.99
  Size2 = 3
  SupportTransform = false
FEATURE [PartDesign::Chamfer] Chamfer004
  Angle = 45
  Base = -> Chamfer003 [Edge250,Edge263,Edge264]
  BaseFeature = -> Chamfer003
  ChamferType = 0
  FlipDirection = false
  Placement = pos=(0,0,0) rot=(0.57735,0.57735,0.57735;2.0944rad)
  Size = 2
  Size2 = 1
  SupportTransform = false
FEATURE [PartDesign::Chamfer] Chamfer005
  Angle = 45
  Base = -> Chamfer004 [Edge345,Edge341,Edge354,Edge374]
  BaseFeature = -> Chamfer004
  ChamferType = 0
  FlipDirection = false
  Placement = pos=(0,0,0) rot=(0.57735,0.57735,0.57735;2.0944rad)
  Size = 7
  Size2 = 1
  SupportTransform = false
FEATURE [PartDesign::Chamfer] Chamfer006
  Angle = 45
  Base = -> Chamfer005 [Edge147,Edge148,Edge149,Edge151,Edge153]
  BaseFeature = -> Chamfer005
  ChamferType = 0
  FlipDirection = false
  Placement = pos=(0,0,0) rot=(0.57735,0.57735,0.57735;2.0944rad)
  Size = 2
  Size2 = 1
  SupportTransform = false
FEATURE [PartDesign::Chamfer] Chamfer007
  Angle = 45
  Base = -> Chamfer006 [Edge109,Edge111,Edge112,Edge114,Edge116]
  BaseFeature = -> Chamfer006
  ChamferType = 0
  FlipDirection = false
  Placement = pos=(0,0,0) rot=(0.57735,0.57735,0.57735;2.0944rad)
  Size = 2
  Size2 = 1
  SupportTransform = false
FEATURE [PartDesign::Fillet] Fillet002
  Base = -> Pocket018 [Face20,Face21]
  BaseFeature = -> Pocket018
  Placement = pos=(-155,4.13e-13,-2.323e-13) rot=(-0.57735,0.57735,0.57735;4.18879rad)
  Radius = 0.4
  SupportTransform = false
FEATURE [PartDesign::Body] Body007  label="FlapsWheelsBaseMount"
  Group = -> [DatumPlane010,CopyPocket016,Sketch029,Pad016,Sketch030,Sketch031,Pad017,Sketch032,Pocket017,Sketch033,Pad018,Sketch034,Pocket018,Fillet002]
  Origin = -> Origin116
  Tip = -> Fillet002
FEATURE [PartDesign::Fillet] Fillet003
  Base = -> Pocket020 [Face20,Face21]
  BaseFeature = -> Pocket020
  Placement = pos=(0,0,0) rot=(0.57735,0.57735,0.57735;2.0944rad)
  Radius = 0.4
  SupportTransform = false
FEATURE [PartDesign::Body] Body008  label="TrimWheelBaseMount"
  Group = -> [DatumPlane011,CopyPocket016001,Sketch035,Pad019,Sketch036,Pad020,Sketch037,Pocket019,Sketch038,Pocket020,Fillet003]
  Origin = -> Origin117
  Tip = -> Fillet003
FEATURE [Sketcher::SketchObject] Sketch041
  FullyConstrained = false
  MapMode = 5
  Placement = pos=(2.88e-14,64.8216,-2.807e-13) rot=(0.57735,0.57735,0.57735;4.18879rad)
  Support = -> [Chamfer007]
  sketch-geometry (1):
    g0: Circle CenterX=-18.1723 CenterY=-129.492 CenterZ=0 NormalX=0 NormalY=0 NormalZ=1 AngleXU=0 Radius=1.5
  constraints (1):
    c: Radius(g0) = 1.5
FEATURE [PartDesign::Pocket] Pocket022
  BaseFeature = -> Chamfer007
  Length = 4
  Length2 = 100
  Placement = pos=(0,0,0) rot=(0.57735,0.57735,0.57735;2.0944rad)
  Profile = -> Sketch041
  Type = 0
FEATURE [PartDesign::Fillet] Fillet004
  Base = -> Pocket022 [Edge118,Edge114,Edge110]
  BaseFeature = -> Pocket022
  Placement = pos=(0,0,0) rot=(0.57735,0.57735,0.57735;2.0944rad)
  Radius = 0.5
  SupportTransform = false
FEATURE [PartDesign::Fillet] Fillet005
  Base = -> Fillet004 [Edge227,Edge223,Edge219]
  BaseFeature = -> Fillet004
  Placement = pos=(0,0,0) rot=(0.57735,0.57735,0.57735;2.0944rad)
  Radius = 0.5
  SupportTransform = false
FEATURE [PartDesign::Fillet] Fillet006
  Base = -> Fillet005 [Edge470]
  BaseFeature = -> Fillet005
  Placement = pos=(0,0,0) rot=(0.57735,0.57735,0.57735;2.0944rad)
  Radius = 1
  SupportTransform = false
FEATURE [PartDesign::Body] Body006  label="CaseFrontv2"
  Group = -> [Sketch018,Pad012,DatumPlane003,Sketch019,Pocket010,DatumPlane004,Sketch020,Pocket011,DatumPlane005,Sketch021,Pocket012,DatumPlane006,Sketch022,Pad013,DatumPlane007,DatumPlane008,Sketch023,Pad014,Sketch024,Pocket013,DatumPlane009,Sketch025,Pocket014,Sketch026,Pocket015,Sketch027,Pad015,Sketch028,Pocket016,DatumPlane012,Sketch039,Pad021,DatumPlane013,DatumPlane014,Sketch040,Pocket021,Chamfer003,+9 more]
  Origin = -> Origin115
  Tip = -> Fillet006
FEATURE [Sketcher::SketchObject] Sketch042
  FullyConstrained = false
  MapMode = 5
  Placement = pos=(0,0,0) rot=(1,0,0;1.5708rad)
  Support = -> [XZ_Plane118]
  sketch-geometry (4):
    g0: LineSegment StartX=-9.77327 StartY=-8.66071 StartZ=0 EndX=-29.7733 EndY=-8.66071 EndZ=0
    g1: LineSegment StartX=-29.7733 StartY=-8.66071 StartZ=0 EndX=-29.7733 EndY=-28.6607 EndZ=0
    g2: LineSegment StartX=-29.7733 StartY=-28.6607 StartZ=0 EndX=-9.77327 EndY=-28.6607 EndZ=0
    g3: LineSegment StartX=-9.77327 StartY=-28.6607 StartZ=0 EndX=-9.77327 EndY=-8.66071 EndZ=0
  constraints (10):
    c: Coincident(g0,g1)
    c: Coincident(g1,g2)
    c: Coincident(g2,g3)
    c: Coincident(g3,g0)
    c: Horizontal(g0)
    c: Horizontal(g2)
    c: Vertical(g1)
    c: Vertical(g3)
    c: Equal(g2,g1)
    c: DistanceX(g0,g0) = 20
FEATURE [PartDesign::Pad] Pad022
  Direction = (1,1,1)
  Length = 9
  Length2 = 100
  Placement = pos=(0,0,0) rot=(1,0,0;1.5708rad)
  Profile = -> Sketch042
  Type = 0
FEATURE [Sketcher::SketchObject] Sketch043
  ExternalGeometry = -> [Pad022]
  FullyConstrained = true
  MapMode = 5
  Placement = pos=(0,-9,6e-15) rot=(1,0,0;1.5708rad)
  Support = -> [Pad022]
  sketch-geometry (3):
    g0: LineSegment StartX=-29.7733 StartY=-28.6607 StartZ=0 EndX=-9.77327 EndY=-8.66071 EndZ=0
    g1: LineSegment StartX=-29.7733 StartY=-8.66071 StartZ=0 EndX=-9.77327 EndY=-28.6607 EndZ=0
    g2: Circle CenterX=-19.7733 CenterY=-18.6607 CenterZ=0 NormalX=0 NormalY=0 NormalZ=1 AngleXU=0 Radius=7
  constraints (7):
    c: Coincident(g0,g-4)
    c: Coincident(g0,g-3)
    c: Coincident(g1,g-3)
    c: Coincident(g1,g-4)
    c: PointOnObject(g2,g0)
    c: PointOnObject(g2,g1)
    c: Radius(g2) = 7
FEATURE [PartDesign::Pad] Pad023
  BaseFeature = -> Pad022
  Direction = (1,1,1)
  Length = 10
  Length2 = 100
  Placement = pos=(0,0,0) rot=(1,0,0;1.5708rad)
  Profile = -> Sketch043
  Type = 0
FEATURE [Sketcher::SketchObject] Sketch044
  ExternalGeometry = -> [Pad023]
  FullyConstrained = false
  MapMode = 5
  Placement = pos=(1.6e-15,-19,2.24e-14) rot=(1,0,0;1.5708rad)
  Support = -> [Pad023]
  sketch-geometry (5):
    g0: Circle CenterX=-19.7733 CenterY=-18.6607 CenterZ=0 NormalX=0 NormalY=0 NormalZ=1 AngleXU=0 Radius=2.65
    g1: LineSegment StartX=-17.1233 StartY=-18.6607 StartZ=0 EndX=-17.1233 EndY=-31.7454 EndZ=0
    g2: LineSegment StartX=-17.1233 StartY=-31.7454 StartZ=0 EndX=-22.4233 EndY=-31.7454 EndZ=0
    g3: LineSegment StartX=-22.4233 StartY=-31.7454 StartZ=0 EndX=-22.4233 EndY=-18.6607 EndZ=0
    g4: ArcOfCircle CenterX=-19.7733 CenterY=-18.6607 CenterZ=0 NormalX=0 NormalY=0 NormalZ=1 AngleXU=0 Radius=2.65 StartAngle=1.68785e-11 EndAngle=3.14159
  constraints (11):
    c: Coincident(g0,g-3)
    c: Radius(g0) = 2.65
    c: Coincident(g1,g2)
    c: Coincident(g2,g3)
    c: Horizontal(g2)
    c: Vertical(g1)
    c: Vertical(g3)
    c: PointOnObject(g3,g0)
    c: Coincident(g4,g0)
    c: Tangent(g3,g4) = 1.5708
    c: Coincident(g1,g4)
FEATURE [PartDesign::Pocket] Pocket023
  BaseFeature = -> Pad023
  Length = 8
  Length2 = 100
  Placement = pos=(0,0,0) rot=(1,0,0;1.5708rad)
  Profile = -> Sketch044
  Type = 0
FEATURE [Sketcher::SketchObject] Sketch045
  ExternalGeometry = -> [Pocket023]
  FullyConstrained = true
  MapMode = 5
  Placement = pos=(0,-4.45e-14,-28.6607) rot=(1,0,0;3.14159rad)
  Support = -> [Pocket023]
FEATURE [Sketcher::SketchObject] Sketch046
  ExternalGeometry = -> [Pocket023]
  FullyConstrained = true
  MapMode = 5
  Placement = pos=(0,-4.45e-14,-28.6607) rot=(1,0,0;3.14159rad)
  Support = -> [Pocket023]
  sketch-geometry (6):
    g0: LineSegment StartX=-24.1483 StartY=9 StartZ=0 EndX=-15.3983 EndY=9 EndZ=0
    g1: LineSegment StartX=-15.3983 StartY=9 StartZ=0 EndX=-15.3983 EndY=14.2 EndZ=0
    g2: LineSegment StartX=-15.3983 StartY=14.2 StartZ=0 EndX=-24.1483 EndY=14.2 EndZ=0
    g3: LineSegment StartX=-24.1483 StartY=14.2 StartZ=0 EndX=-24.1483 EndY=9 EndZ=0
    g4: LineSegment StartX=-24.1483 StartY=14.2 StartZ=0 EndX=-29.7733 EndY=9 EndZ=0
    g5: LineSegment StartX=-15.3983 StartY=14.2 StartZ=0 EndX=-9.77327 EndY=9 EndZ=0
  constraints (16):
    c: Coincident(g0,g1)
    c: Coincident(g1,g2)
    c: Coincident(g2,g3)
    c: Coincident(g3,g0)
    c: Horizontal(g0)
    c: Horizontal(g2)
    c: Vertical(g1)
    c: Vertical(g3)
    c: PointOnObject(g0,g-3)
    c: DistanceY(g3,g3) = 5.2
    c: DistanceX(g2,g2) = 8.75
    c: Coincident(g4,g2)
    c: Coincident(g4,g-3)
    c: Coincident(g5,g1)
    c: Coincident(g5,g-3)
    c: Equal(g5,g4)
FEATURE [PartDesign::Pocket] Pocket024
  BaseFeature = -> Pocket023
  Length = 1
  Length2 = 100
  Placement = pos=(0,0,0) rot=(1,0,0;1.5708rad)
  Profile = -> Sketch046
  Type = 0
FEATURE [Sketcher::SketchObject] Sketch047
  ExternalGeometry = -> [Pocket024]
  FullyConstrained = true
  MapMode = 5
  Placement = pos=(0,0,0) rot=(-1,0,0;1.5708rad)
  Support = -> [Pocket024]
  sketch-geometry (3):
    g0: LineSegment StartX=-29.7733 StartY=28.6607 StartZ=0 EndX=-9.77327 EndY=8.66071 EndZ=0
    g1: LineSegment StartX=-29.7733 StartY=8.66071 StartZ=0 EndX=-9.77327 EndY=28.6607 EndZ=0
    g2: Circle CenterX=-19.7733 CenterY=18.6607 CenterZ=0 NormalX=0 NormalY=0 NormalZ=1 AngleXU=0 Radius=3.7
  constraints (7):
    c: Coincident(g0,g-3)
    c: Coincident(g0,g-4)
    c: Coincident(g1,g-5)
    c: Coincident(g1,g-4)
    c: PointOnObject(g2,g0)
    c: PointOnObject(g2,g1)
    c: Radius(g2) = 3.7
FEATURE [PartDesign::Pocket] Pocket025
  BaseFeature = -> Pocket024
  Length = 3
  Length2 = 100
  Placement = pos=(0,0,0) rot=(1,0,0;1.5708rad)
  Profile = -> Sketch047
  Type = 0
FEATURE [Sketcher::SketchObject] Sketch048
  ExternalGeometry = -> [Pocket025]
  FullyConstrained = true
  MapMode = 5
  Placement = pos=(1.6e-15,-19,4.77e-14) rot=(1,0,0;1.5708rad)
  Support = -> [Pocket025]
  sketch-geometry (1):
    g0: Circle CenterX=-19.7733 CenterY=-18.6607 CenterZ=0 NormalX=0 NormalY=0 NormalZ=1 AngleXU=0 Radius=1.675
  constraints (2):
    c: Coincident(g0,g-3)
    c: Radius(g0) = 1.675
FEATURE [PartDesign::Pocket] Pocket026
  BaseFeature = -> Pocket025
  Length = 5
  Length2 = 100
  Placement = pos=(0,0,0) rot=(1,0,0;1.5708rad)
  Profile = -> Sketch048
  Type = 0
FEATURE [PartDesign::Fillet] Fillet007
  Base = -> Pocket026 [Face4,Face2,Face6,Face3,Face1]
  BaseFeature = -> Pocket026
  Placement = pos=(0,0,0) rot=(1,0,0;1.5708rad)
  Radius = 2
  SupportTransform = false
FEATURE [Sketcher::SketchObject] Sketch057
  AttachmentOffset = pos=(0,0,-4.8) rot=(0,0,1;0rad)
  ExternalGeometry = -> [Fillet007]
  FullyConstrained = true
  MapMode = 5
  Placement = pos=(1.2e-15,-14.2,3.62e-14) rot=(1,0,0;1.5708rad)
  Support = -> [Fillet007]
  sketch-geometry (6):
    g0: ArcOfCircle CenterX=-19.7733 CenterY=-18.6607 CenterZ=0 NormalX=0 NormalY=0 NormalZ=1 AngleXU=0 Radius=4.4 StartAngle=1.01652e-11 EndAngle=3.14159
    g1: LineSegment StartX=-24.1733 StartY=-18.6607 StartZ=0 EndX=-24.1733 EndY=-31.355 EndZ=0
    g2: LineSegment StartX=-24.1733 StartY=-31.355 StartZ=0 EndX=-15.3733 EndY=-31.355 EndZ=0
    g3: LineSegment StartX=-15.3733 StartY=-18.6607 StartZ=0 EndX=-15.3733 EndY=-31.355 EndZ=0
    g4: LineSegment StartX=-22.4233 StartY=-18.6607 StartZ=0 EndX=-24.1733 EndY=-18.6607 EndZ=0
    g5: LineSegment StartX=-17.1233 StartY=-18.6607 StartZ=0 EndX=-15.3733 EndY=-18.6607 EndZ=0
  constraints (16):
    c: Coincident(g0,g-3)
    c: Coincident(g1,g0)
    c: Vertical(g1)
    c: Coincident(g2,g1)
    c: Coincident(g3,g0)
    c: Coincident(g3,g2)
    c: Vertical(g3)
    c: Horizontal(g2)
    c: Coincident(g4,g-3)
    c: Coincident(g4,g0)
    c: Horizontal(g4)
    c: Coincident(g5,g-3)
    c: Coincident(g5,g0)
    c: Horizontal(g5)
    c: Equal(g5,g4)
    c: Radius(g0) = 4.4
FEATURE [PartDesign::Pocket] Pocket033
  BaseFeature = -> Fillet007
  Length = 5.2
  Length2 = 100
  Placement = pos=(0,0,0) rot=(1,0,0;1.5708rad)
  Profile = -> Sketch057
  Type = 0
FEATURE [Sketcher::SketchObject] Sketch058
  ExternalGeometry = -> [Pocket033]
  FullyConstrained = true
  MapMode = 5
  Placement = pos=(0,-3,8.7e-15) rot=(-1,0,0;1.5708rad)
  Support = -> [Pocket033]
  sketch-geometry (1):
    g0: Circle CenterX=-19.7733 CenterY=18.6607 CenterZ=0 NormalX=0 NormalY=0 NormalZ=1 AngleXU=0 Radius=1.7
  constraints (2):
    c: Coincident(g0,g-3)
    c: Radius(g0) = 1.7
FEATURE [PartDesign::Pocket] Pocket034
  BaseFeature = -> Pocket033
  Length = 10
  Length2 = 100
  Placement = pos=(0,0,0) rot=(1,0,0;1.5708rad)
  Profile = -> Sketch058
  Type = 0
FEATURE [PartDesign::Body] Body009  label="CarburatorHead"
  Group = -> [Sketch042,Pad022,Sketch043,Pad023,Sketch044,Pocket023,Sketch045,Sketch046,Pocket024,Sketch047,Pocket025,Sketch048,Pocket026,Fillet007,Sketch057,Pocket033,Sketch058,Pocket034]
  Origin = -> Origin118
  Tip = -> Pocket034
FEATURE [Sketcher::SketchObject] Sketch062
  FullyConstrained = false
  MapMode = 5
  Placement = pos=(0,-3,7e-15) rot=(-1,0,0;1.5708rad)
  sketch-geometry (1):
    g0: Circle CenterX=-19.7733 CenterY=18.6607 CenterZ=0 NormalX=0 NormalY=0 NormalZ=1 AngleXU=0 Radius=1.7
  constraints (1):
    c: Radius(g0) = 1.7
FEATURE [Sketcher::SketchObject] Sketch064
  AttachmentOffset = pos=(0,0,-4.8) rot=(0,0,1;0rad)
  FullyConstrained = false
  MapMode = 5
  Placement = pos=(1.1e-15,-14.2,1.46e-14) rot=(1,0,0;1.5708rad)
  sketch-geometry (6):
    g0: ArcOfCircle CenterX=-19.7733 CenterY=-18.6607 CenterZ=0 NormalX=0 NormalY=0 NormalZ=1 AngleXU=0 Radius=4.4 StartAngle=1.01652e-11 EndAngle=3.14159
    g1: LineSegment StartX=-24.1733 StartY=-18.6607 StartZ=0 EndX=-24.1733 EndY=-31.355 EndZ=0
    g2: LineSegment StartX=-24.1733 StartY=-31.355 StartZ=0 EndX=-15.3733 EndY=-31.355 EndZ=0
    g3: LineSegment StartX=-15.3733 StartY=-18.6607 StartZ=0 EndX=-15.3733 EndY=-31.355 EndZ=0
    g4: LineSegment StartX=-22.4233 StartY=-18.6607 StartZ=0 EndX=-24.1733 EndY=-18.6607 EndZ=0
    g5: LineSegment StartX=-17.1233 StartY=-18.6607 StartZ=0 EndX=-15.3733 EndY=-18.6607 EndZ=0
  constraints (13):
    c: Coincident(g1,g0)
    c: Vertical(g1)
    c: Coincident(g2,g1)
    c: Coincident(g3,g0)
    c: Coincident(g3,g2)
    c: Vertical(g3)
    c: Horizontal(g2)
    c: Coincident(g4,g0)
    c: Horizontal(g4)
    c: Coincident(g5,g0)
    c: Horizontal(g5)
    c: Equal(g5,g4)
    c: Radius(g0) = 4.4
FEATURE [Sketcher::SketchObject] Sketch067
  FullyConstrained = false
  MapMode = 5
  Placement = pos=(0,0,0) rot=(1,0,0;1.5708rad)
  Support = -> [XZ_Plane119]
  sketch-geometry (4):
    g0: LineSegment StartX=-9.77327 StartY=-8.66071 StartZ=0 EndX=-29.7733 EndY=-8.66071 EndZ=0
    g1: LineSegment StartX=-29.7733 StartY=-8.66071 StartZ=0 EndX=-29.7733 EndY=-28.6607 EndZ=0
    g2: LineSegment StartX=-29.7733 StartY=-28.6607 StartZ=0 EndX=-9.77327 EndY=-28.6607 EndZ=0
    g3: LineSegment StartX=-9.77327 StartY=-28.6607 StartZ=0 EndX=-9.77327 EndY=-8.66071 EndZ=0
  constraints (10):
    c: Coincident(g0,g1)
    c: Coincident(g1,g2)
    c: Coincident(g2,g3)
    c: Coincident(g3,g0)
    c: Horizontal(g0)
    c: Horizontal(g2)
    c: Vertical(g1)
    c: Vertical(g3)
    c: Equal(g2,g1)
    c: DistanceX(g0,g0) = 20
FEATURE [PartDesign::Pad] Pad025
  Direction = (1,1,1)
  Length = 9
  Length2 = 100
  Placement = pos=(0,0,0) rot=(1,0,0;1.5708rad)
  Profile = -> Sketch067
  Type = 0
FEATURE [Sketcher::SketchObject] Sketch061
  ExternalGeometry = -> [Pad025]
  FullyConstrained = true
  MapMode = 5
  Placement = pos=(0,-9,4e-15) rot=(1,0,0;1.5708rad)
  Support = -> [Pad025]
  sketch-geometry (3):
    g0: LineSegment StartX=-29.7733 StartY=-28.6607 StartZ=0 EndX=-9.77327 EndY=-8.66071 EndZ=0
    g1: LineSegment StartX=-29.7733 StartY=-8.66071 StartZ=0 EndX=-9.77327 EndY=-28.6607 EndZ=0
    g2: Circle CenterX=-19.7733 CenterY=-18.6607 CenterZ=0 NormalX=0 NormalY=0 NormalZ=1 AngleXU=0 Radius=7
  constraints (7):
    c: Coincident(g0,g-4)
    c: Coincident(g0,g-3)
    c: Coincident(g1,g-3)
    c: Coincident(g1,g-4)
    c: PointOnObject(g2,g0)
    c: PointOnObject(g2,g1)
    c: Radius(g2) = 7
FEATURE [PartDesign::Pad] Pad024
  BaseFeature = -> Pad025
  Direction = (1,1,1)
  Length = 10
  Length2 = 100
  Placement = pos=(0,0,0) rot=(1,0,0;1.5708rad)
  Profile = -> Sketch061
  Type = 0
FEATURE [Sketcher::SketchObject] Sketch065
  ExternalGeometry = -> [Pad024]
  FullyConstrained = false
  MapMode = 5
  Placement = pos=(1.5e-15,-19,1.81e-14) rot=(1,0,0;1.5708rad)
  Support = -> [Pad024]
  sketch-geometry (5):
    g0: Circle CenterX=-19.7733 CenterY=-18.6607 CenterZ=0 NormalX=0 NormalY=0 NormalZ=1 AngleXU=0 Radius=2.65
    g1: LineSegment StartX=-17.1233 StartY=-18.6607 StartZ=0 EndX=-17.1233 EndY=-31.7454 EndZ=0
    g2: LineSegment StartX=-17.1233 StartY=-31.7454 StartZ=0 EndX=-22.4233 EndY=-31.7454 EndZ=0
    g3: LineSegment StartX=-22.4233 StartY=-31.7454 StartZ=0 EndX=-22.4233 EndY=-18.6607 EndZ=0
    g4: ArcOfCircle CenterX=-19.7733 CenterY=-18.6607 CenterZ=0 NormalX=0 NormalY=0 NormalZ=1 AngleXU=0 Radius=2.65 StartAngle=1.68785e-11 EndAngle=3.14159
  constraints (11):
    c: Coincident(g0,g-3)
    c: Radius(g0) = 2.65
    c: Coincident(g1,g2)
    c: Coincident(g2,g3)
    c: Horizontal(g2)
    c: Vertical(g1)
    c: Vertical(g3)
    c: PointOnObject(g3,g0)
    c: Coincident(g4,g0)
    c: Tangent(g3,g4) = 1.5708
    c: Coincident(g1,g4)
FEATURE [PartDesign::Pocket] Pocket040
  BaseFeature = -> Pad024
  Length = 8
  Length2 = 100
  Placement = pos=(0,0,0) rot=(1,0,0;1.5708rad)
  Profile = -> Sketch065
  Type = 0
FEATURE [Sketcher::SketchObject] Sketch063
  ExternalGeometry = -> [Pocket040]
  FullyConstrained = true
  MapMode = 5
  Placement = pos=(0,-1.9e-14,-28.6607) rot=(1,0,0;3.14159rad)
  Support = -> [Pocket040]
  sketch-geometry (6):
    g0: LineSegment StartX=-24.1483 StartY=9 StartZ=0 EndX=-15.3983 EndY=9 EndZ=0
    g1: LineSegment StartX=-15.3983 StartY=9 StartZ=0 EndX=-15.3983 EndY=14.2 EndZ=0
    g2: LineSegment StartX=-15.3983 StartY=14.2 StartZ=0 EndX=-24.1483 EndY=14.2 EndZ=0
    g3: LineSegment StartX=-24.1483 StartY=14.2 StartZ=0 EndX=-24.1483 EndY=9 EndZ=0
    g4: LineSegment StartX=-24.1483 StartY=14.2 StartZ=0 EndX=-29.7733 EndY=9 EndZ=0
    g5: LineSegment StartX=-15.3983 StartY=14.2 StartZ=0 EndX=-9.77327 EndY=9 EndZ=0
  constraints (16):
    c: Coincident(g0,g1)
    c: Coincident(g1,g2)
    c: Coincident(g2,g3)
    c: Coincident(g3,g0)
    c: Horizontal(g0)
    c: Horizontal(g2)
    c: Vertical(g1)
    c: Vertical(g3)
    c: PointOnObject(g0,g-3)
    c: DistanceY(g3,g3) = 5.2
    c: DistanceX(g2,g2) = 8.75
    c: Coincident(g4,g2)
    c: Coincident(g4,g-3)
    c: Coincident(g5,g1)
    c: Coincident(g5,g-3)
    c: Equal(g5,g4)
FEATURE [PartDesign::Pocket] Pocket036
  BaseFeature = -> Pocket040
  Length = 1
  Length2 = 100
  Placement = pos=(0,0,0) rot=(1,0,0;1.5708rad)
  Profile = -> Sketch063
  Type = 0
FEATURE [Sketcher::SketchObject] Sketch060
  ExternalGeometry = -> [Pocket036]
  FullyConstrained = true
  MapMode = 5
  Placement = pos=(0,0,0) rot=(-1,0,0;1.5708rad)
  Support = -> [Pocket036]
  sketch-geometry (3):
    g0: LineSegment StartX=-29.7733 StartY=28.6607 StartZ=0 EndX=-9.77327 EndY=8.66071 EndZ=0
    g1: LineSegment StartX=-29.7733 StartY=8.66071 StartZ=0 EndX=-9.77327 EndY=28.6607 EndZ=0
    g2: Circle CenterX=-19.7733 CenterY=18.6607 CenterZ=0 NormalX=0 NormalY=0 NormalZ=1 AngleXU=0 Radius=3.7
  constraints (7):
    c: Coincident(g0,g-3)
    c: Coincident(g0,g-4)
    c: Coincident(g1,g-5)
    c: Coincident(g1,g-4)
    c: PointOnObject(g2,g0)
    c: PointOnObject(g2,g1)
    c: Radius(g2) = 3.7
FEATURE [PartDesign::Pocket] Pocket035
  BaseFeature = -> Pocket036
  Length = 3
  Length2 = 100
  Placement = pos=(0,0,0) rot=(1,0,0;1.5708rad)
  Profile = -> Sketch060
  Type = 0
FEATURE [Sketcher::SketchObject] Sketch059
  ExternalGeometry = -> [Pocket035]
  FullyConstrained = true
  MapMode = 5
  Placement = pos=(1.5e-15,-19,1.81e-14) rot=(1,0,0;1.5708rad)
  Support = -> [Pocket035]
  sketch-geometry (1):
    g0: Circle CenterX=-19.7733 CenterY=-18.6607 CenterZ=0 NormalX=0 NormalY=0 NormalZ=1 AngleXU=0 Radius=1.675
  constraints (2):
    c: Coincident(g0,g-3)
    c: Radius(g0) = 1.675
FEATURE [Sketcher::SketchObject] Sketch066
  ExternalGeometry = -> [Pocket040]
  FullyConstrained = true
  MapMode = 5
  Placement = pos=(0,-1.9e-14,-28.6607) rot=(1,0,0;3.14159rad)
  Support = -> [Pocket040]
FEATURE [PartDesign::Pocket] Pocket039
  BaseFeature = -> Pocket035
  Length = 5
  Length2 = 100
  Placement = pos=(0,0,0) rot=(1,0,0;1.5708rad)
  Profile = -> Sketch059
  Type = 0
FEATURE [Sketcher::SketchObject] Sketch068
  ExternalGeometry = -> [Pocket039]
  FullyConstrained = false
  MapMode = 5
  Placement = pos=(0,0,0) rot=(-1,0,0;1.5708rad)
  Support = -> [Pocket039]
  sketch-geometry (2):
    g0: Circle CenterX=-19.7733 CenterY=18.6607 CenterZ=0 NormalX=0 NormalY=0 NormalZ=1 AngleXU=0 Radius=16.7549
    g1: Circle CenterX=-19.7733 CenterY=18.6607 CenterZ=0 NormalX=0 NormalY=0 NormalZ=1 AngleXU=0 Radius=9.77178
  constraints (2):
    c: Coincident(g0,g-3)
    c: Coincident(g1,g0)
FEATURE [PartDesign::Pocket] Pocket041
  BaseFeature = -> Pocket039
  Length = 20
  Length2 = 100
  Placement = pos=(0,0,0) rot=(1,0,0;1.5708rad)
  Profile = -> Sketch068
  Type = 0
FEATURE [PartDesign::Pocket] Pocket042
  BaseFeature = -> Pocket041
  Length = 20
  Length2 = 100
  Placement = pos=(0,0,0) rot=(1,0,0;1.5708rad)
  Profile = -> Sketch062
  Type = 0
FEATURE [PartDesign::Fillet] Fillet008
  Base = -> Pocket042 [Face4,Face1]
  BaseFeature = -> Pocket042
  Placement = pos=(0,0,0) rot=(1,0,0;1.5708rad)
  Radius = 1.2
  SupportTransform = false
FEATURE [PartDesign::Pocket] Pocket043
  BaseFeature = -> Fillet008
  Length = 5.2
  Length2 = 100
  Placement = pos=(0,0,0) rot=(1,0,0;1.5708rad)
  Profile = -> Sketch064
  Type = 0
FEATURE [PartDesign::Body] Body010  label="ThrottleHead"
  Group = -> [Sketch067,Pad025,Sketch061,Pad024,Sketch065,Pocket040,Sketch066,Sketch063,Pocket036,Sketch060,Pocket035,Sketch059,Pocket039,Sketch064,Sketch062,Sketch068,Pocket041,Pocket042,Fillet008,Pocket043]
  Origin = -> Origin119
  Tip = -> Pocket043
FEATURE [Sketcher::SketchObject] Sketch070
  AttachmentOffset = pos=(0,0,-4.8) rot=(0,0,1;0rad)
  FullyConstrained = false
  MapMode = 5
  Placement = pos=(1e-15,-14.2,1.5e-14) rot=(1,0,0;1.5708rad)
  sketch-geometry (6):
    g0: ArcOfCircle CenterX=-19.7733 CenterY=-18.6607 CenterZ=0 NormalX=0 NormalY=0 NormalZ=1 AngleXU=0 Radius=4.4 StartAngle=1.01652e-11 EndAngle=3.14159
    g1: LineSegment StartX=-24.1733 StartY=-18.6607 StartZ=0 EndX=-24.1733 EndY=-31.355 EndZ=0
    g2: LineSegment StartX=-24.1733 StartY=-31.355 StartZ=0 EndX=-15.3733 EndY=-31.355 EndZ=0
    g3: LineSegment StartX=-15.3733 StartY=-18.6607 StartZ=0 EndX=-15.3733 EndY=-31.355 EndZ=0
    g4: LineSegment StartX=-22.4233 StartY=-18.6607 StartZ=0 EndX=-24.1733 EndY=-18.6607 EndZ=0
    g5: LineSegment StartX=-17.1233 StartY=-18.6607 StartZ=0 EndX=-15.3733 EndY=-18.6607 EndZ=0
  constraints (13):
    c: Coincident(g1,g0)
    c: Vertical(g1)
    c: Coincident(g2,g1)
    c: Coincident(g3,g0)
    c: Coincident(g3,g2)
    c: Vertical(g3)
    c: Horizontal(g2)
    c: Coincident(g4,g0)
    c: Horizontal(g4)
    c: Coincident(g5,g0)
    c: Horizontal(g5)
    c: Equal(g5,g4)
    c: Radius(g0) = 4.4
FEATURE [Sketcher::SketchObject] Sketch072
  FullyConstrained = false
  MapMode = 5
  Placement = pos=(0,0,0) rot=(1,0,0;1.5708rad)
  Support = -> [XZ_Plane120]
  sketch-geometry (4):
    g0: LineSegment StartX=-9.77327 StartY=-8.66071 StartZ=0 EndX=-29.7733 EndY=-8.66071 EndZ=0
    g1: LineSegment StartX=-29.7733 StartY=-8.66071 StartZ=0 EndX=-29.7733 EndY=-28.6607 EndZ=0
    g2: LineSegment StartX=-29.7733 StartY=-28.6607 StartZ=0 EndX=-9.77327 EndY=-28.6607 EndZ=0
    g3: LineSegment StartX=-9.77327 StartY=-28.6607 StartZ=0 EndX=-9.77327 EndY=-8.66071 EndZ=0
  constraints (10):
    c: Coincident(g0,g1)
    c: Coincident(g1,g2)
    c: Coincident(g2,g3)
    c: Coincident(g3,g0)
    c: Horizontal(g0)
    c: Horizontal(g2)
    c: Vertical(g1)
    c: Vertical(g3)
    c: Equal(g2,g1)
    c: DistanceX(g0,g0) = 20
FEATURE [PartDesign::Pad] Pad026
  Direction = (1,1,1)
  Length = 9
  Length2 = 100
  Placement = pos=(0,0,0) rot=(1,0,0;1.5708rad)
  Profile = -> Sketch072
  Type = 0
FEATURE [Sketcher::SketchObject] Sketch075
  ExternalGeometry = -> [Pad026]
  FullyConstrained = true
  MapMode = 5
  Placement = pos=(0,-9,2e-15) rot=(1,0,0;1.5708rad)
  Support = -> [Pad026]
  sketch-geometry (3):
    g0: LineSegment StartX=-29.7733 StartY=-28.6607 StartZ=0 EndX=-9.77327 EndY=-8.66071 EndZ=0
    g1: LineSegment StartX=-29.7733 StartY=-8.66071 StartZ=0 EndX=-9.77327 EndY=-28.6607 EndZ=0
    g2: Circle CenterX=-19.7733 CenterY=-18.6607 CenterZ=0 NormalX=0 NormalY=0 NormalZ=1 AngleXU=0 Radius=7
  constraints (7):
    c: Coincident(g0,g-4)
    c: Coincident(g0,g-3)
    c: Coincident(g1,g-3)
    c: Coincident(g1,g-4)
    c: PointOnObject(g2,g0)
    c: PointOnObject(g2,g1)
    c: Radius(g2) = 7
FEATURE [Sketcher::SketchObject] Sketch076
  FullyConstrained = false
  MapMode = 5
  Placement = pos=(0,-3,7e-15) rot=(-1,0,0;1.5708rad)
  sketch-geometry (1):
    g0: Circle CenterX=-19.7733 CenterY=18.6607 CenterZ=0 NormalX=0 NormalY=0 NormalZ=1 AngleXU=0 Radius=1.7
  constraints (1):
    c: Radius(g0) = 1.7
FEATURE [PartDesign::Pad] Pad027
  BaseFeature = -> Pad026
  Direction = (1,1,1)
  Length = 10
  Length2 = 100
  Placement = pos=(0,0,0) rot=(1,0,0;1.5708rad)
  Profile = -> Sketch075
  Type = 0
FEATURE [Sketcher::SketchObject] Sketch071
  ExternalGeometry = -> [Pad027]
  FullyConstrained = false
  MapMode = 5
  Placement = pos=(1.5e-15,-19,1.39e-14) rot=(1,0,0;1.5708rad)
  Support = -> [Pad027]
  sketch-geometry (5):
    g0: Circle CenterX=-19.7733 CenterY=-18.6607 CenterZ=0 NormalX=0 NormalY=0 NormalZ=1 AngleXU=0 Radius=2.65
    g1: LineSegment StartX=-17.1233 StartY=-18.6607 StartZ=0 EndX=-17.1233 EndY=-31.7454 EndZ=0
    g2: LineSegment StartX=-17.1233 StartY=-31.7454 StartZ=0 EndX=-22.4233 EndY=-31.7454 EndZ=0
    g3: LineSegment StartX=-22.4233 StartY=-31.7454 StartZ=0 EndX=-22.4233 EndY=-18.6607 EndZ=0
    g4: ArcOfCircle CenterX=-19.7733 CenterY=-18.6607 CenterZ=0 NormalX=0 NormalY=0 NormalZ=1 AngleXU=0 Radius=2.65 StartAngle=1.68785e-11 EndAngle=3.14159
  constraints (11):
    c: Coincident(g0,g-3)
    c: Radius(g0) = 2.65
    c: Coincident(g1,g2)
    c: Coincident(g2,g3)
    c: Horizontal(g2)
    c: Vertical(g1)
    c: Vertical(g3)
    c: PointOnObject(g3,g0)
    c: Coincident(g4,g0)
    c: Tangent(g3,g4) = 1.5708
    c: Coincident(g1,g4)
FEATURE [PartDesign::Pocket] Pocket046
  BaseFeature = -> Pad027
  Length = 8
  Length2 = 100
  Placement = pos=(0,0,0) rot=(1,0,0;1.5708rad)
  Profile = -> Sketch071
  Type = 0
FEATURE [Sketcher::SketchObject] Sketch069
  ExternalGeometry = -> [Pocket046]
  FullyConstrained = true
  MapMode = 5
  Placement = pos=(0,-1.26e-14,-28.6607) rot=(1,0,0;3.14159rad)
  Support = -> [Pocket046]
FEATURE [Sketcher::SketchObject] Sketch078
  ExternalGeometry = -> [Pocket046]
  FullyConstrained = true
  MapMode = 5
  Placement = pos=(0,-1.26e-14,-28.6607) rot=(1,0,0;3.14159rad)
  Support = -> [Pocket046]
  sketch-geometry (6):
    g0: LineSegment StartX=-24.1483 StartY=9 StartZ=0 EndX=-15.3983 EndY=9 EndZ=0
    g1: LineSegment StartX=-15.3983 StartY=9 StartZ=0 EndX=-15.3983 EndY=14.2 EndZ=0
    g2: LineSegment StartX=-15.3983 StartY=14.2 StartZ=0 EndX=-24.1483 EndY=14.2 EndZ=0
    g3: LineSegment StartX=-24.1483 StartY=14.2 StartZ=0 EndX=-24.1483 EndY=9 EndZ=0
    g4: LineSegment StartX=-24.1483 StartY=14.2 StartZ=0 EndX=-29.7733 EndY=9 EndZ=0
    g5: LineSegment StartX=-15.3983 StartY=14.2 StartZ=0 EndX=-9.77327 EndY=9 EndZ=0
  constraints (16):
    c: Coincident(g0,g1)
    c: Coincident(g1,g2)
    c: Coincident(g2,g3)
    c: Coincident(g3,g0)
    c: Horizontal(g0)
    c: Horizontal(g2)
    c: Vertical(g1)
    c: Vertical(g3)
    c: PointOnObject(g0,g-3)
    c: DistanceY(g3,g3) = 5.2
    c: DistanceX(g2,g2) = 8.75
    c: Coincident(g4,g2)
    c: Coincident(g4,g-3)
    c: Coincident(g5,g1)
    c: Coincident(g5,g-3)
    c: Equal(g5,g4)
FEATURE [PartDesign::Pocket] Pocket045
  BaseFeature = -> Pocket046
  Length = 1
  Length2 = 100
  Placement = pos=(0,0,0) rot=(1,0,0;1.5708rad)
  Profile = -> Sketch078
  Type = 0
FEATURE [Sketcher::SketchObject] Sketch073
  ExternalGeometry = -> [Pocket045]
  FullyConstrained = true
  MapMode = 5
  Placement = pos=(0,0,0) rot=(-1,0,0;1.5708rad)
  Support = -> [Pocket045]
  sketch-geometry (3):
    g0: LineSegment StartX=-29.7733 StartY=28.6607 StartZ=0 EndX=-9.77327 EndY=8.66071 EndZ=0
    g1: LineSegment StartX=-29.7733 StartY=8.66071 StartZ=0 EndX=-9.77327 EndY=28.6607 EndZ=0
    g2: Circle CenterX=-19.7733 CenterY=18.6607 CenterZ=0 NormalX=0 NormalY=0 NormalZ=1 AngleXU=0 Radius=3.7
  constraints (7):
    c: Coincident(g0,g-3)
    c: Coincident(g0,g-4)
    c: Coincident(g1,g-5)
    c: Coincident(g1,g-4)
    c: PointOnObject(g2,g0)
    c: PointOnObject(g2,g1)
    c: Radius(g2) = 3.7
FEATURE [PartDesign::Pocket] Pocket050
  BaseFeature = -> Pocket045
  Length = 3
  Length2 = 100
  Placement = pos=(0,0,0) rot=(1,0,0;1.5708rad)
  Profile = -> Sketch073
  Type = 0
FEATURE [Sketcher::SketchObject] Sketch077
  ExternalGeometry = -> [Pocket050]
  FullyConstrained = true
  MapMode = 5
  Placement = pos=(1.5e-15,-19,1.39e-14) rot=(1,0,0;1.5708rad)
  Support = -> [Pocket050]
  sketch-geometry (1):
    g0: Circle CenterX=-19.7733 CenterY=-18.6607 CenterZ=0 NormalX=0 NormalY=0 NormalZ=1 AngleXU=0 Radius=1.675
  constraints (2):
    c: Coincident(g0,g-3)
    c: Radius(g0) = 1.675
FEATURE [PartDesign::Pocket] Pocket049
  BaseFeature = -> Pocket050
  Length = 5
  Length2 = 100
  Placement = pos=(0,0,0) rot=(1,0,0;1.5708rad)
  Profile = -> Sketch077
  Type = 0
FEATURE [Sketcher::SketchObject] Sketch074
  ExternalGeometry = -> [Pocket049]
  FullyConstrained = false
  MapMode = 5
  Placement = pos=(0,0,0) rot=(-1,0,0;1.5708rad)
  Support = -> [Pocket049]
  sketch-geometry (2):
    g0: Circle CenterX=-19.7733 CenterY=18.6607 CenterZ=0 NormalX=0 NormalY=0 NormalZ=1 AngleXU=0 Radius=16.7549
    g1: Circle CenterX=-19.7733 CenterY=18.6607 CenterZ=0 NormalX=0 NormalY=0 NormalZ=1 AngleXU=0 Radius=9.77178
  constraints (2):
    c: Coincident(g0,g-3)
    c: Coincident(g1,g0)
FEATURE [PartDesign::Pocket] Pocket047
  BaseFeature = -> Pocket049
  Length = 20
  Length2 = 100
  Placement = pos=(0,0,0) rot=(1,0,0;1.5708rad)
  Profile = -> Sketch074
  Type = 0
FEATURE [PartDesign::Pocket] Pocket048
  BaseFeature = -> Pocket047
  Length = 20
  Length2 = 100
  Placement = pos=(0,0,0) rot=(1,0,0;1.5708rad)
  Profile = -> Sketch076
  Type = 0
FEATURE [Sketcher::SketchObject] Sketch079
  ExternalGeometry = -> [Pocket048]
  FullyConstrained = false
  MapMode = 5
  Placement = pos=(0,0,0) rot=(-1,0,0;1.5708rad)
  Support = -> [Pocket048]
  sketch-geometry (4):
    g0: ArcOfCircle CenterX=-19.7733 CenterY=28.1188 CenterZ=0 NormalX=0 NormalY=0 NormalZ=1 AngleXU=0 Radius=0.929393 StartAngle=0.298402 EndAngle=2.84319
    g1: LineSegment StartX=-20.6616 StartY=28.392 StartZ=0 EndX=-20.6616 EndY=27.5889 EndZ=0
    g2: LineSegment StartX=-20.6616 StartY=27.5889 StartZ=0 EndX=-18.885 EndY=27.5889 EndZ=0
    g3: LineSegment StartX=-18.885 StartY=27.5889 StartZ=0 EndX=-18.885 EndY=28.392 EndZ=0
  constraints (10):
    c: DistanceX(g0,g-3) = 0
    c: DistanceY(g0,g0) = 0
    c: PointOnObject(g0,g-3)
    c: Coincident(g1,g0)
    c: Vertical(g1)
    c: Coincident(g2,g1)
    c: Horizontal(g2)
    c: Coincident(g3,g2)
    c: Coincident(g3,g0)
    c: Vertical(g3)
FEATURE [PartDesign::Pad] Pad028
  BaseFeature = -> Pocket048
  Direction = (1,1,1)
  Length = 9
  Length2 = 100
  Placement = pos=(0,0,0) rot=(1,0,0;1.5708rad)
  Profile = -> Sketch079
  Reversed = true
  Type = 0
FEATURE [PartDesign::Line] DatumLine
  AttacherType = Attacher::AttachEngineLine
  Length = 20
  MapMode = 19
  Placement = pos=(-19.7733,-3.94e-14,-18.6607) rot=(-1,0,0;1.5708rad)
  ResizeMode = 0
  Support = -> [Pad028]
FEATURE [PartDesign::PolarPattern] PolarPattern
  Angle = 360
  Axis = -> DatumLine
  BaseFeature = -> Pad028
  Occurrences = 8
  Originals = -> [Pad028]
  Placement = pos=(0,0,0) rot=(1,0,0;1.5708rad)
FEATURE [PartDesign::Fillet] Fillet009
  Base = -> PolarPattern [Edge99]
  BaseFeature = -> PolarPattern
  Placement = pos=(0,0,0) rot=(1,0,0;1.5708rad)
  Radius = 1.4
  SupportTransform = false
FEATURE [PartDesign::Pocket] Pocket051
  BaseFeature = -> Fillet009
  Length = 5.2
  Length2 = 100
  Placement = pos=(0,0,0) rot=(1,0,0;1.5708rad)
  Profile = -> Sketch070
  Type = 0
FEATURE [PartDesign::Body] Body011  label="MixtureHead"
  Group = -> [Sketch072,Pad026,Sketch075,Pad027,Sketch071,Pocket046,Sketch069,Sketch078,Pocket045,Sketch073,Pocket050,Sketch077,Pocket049,Sketch070,Sketch076,Sketch074,Pocket047,Pocket048,Sketch079,Pad028,DatumLine,PolarPattern,Fillet009,Pocket051]
  Origin = -> Origin120
  Tip = -> Pocket051
